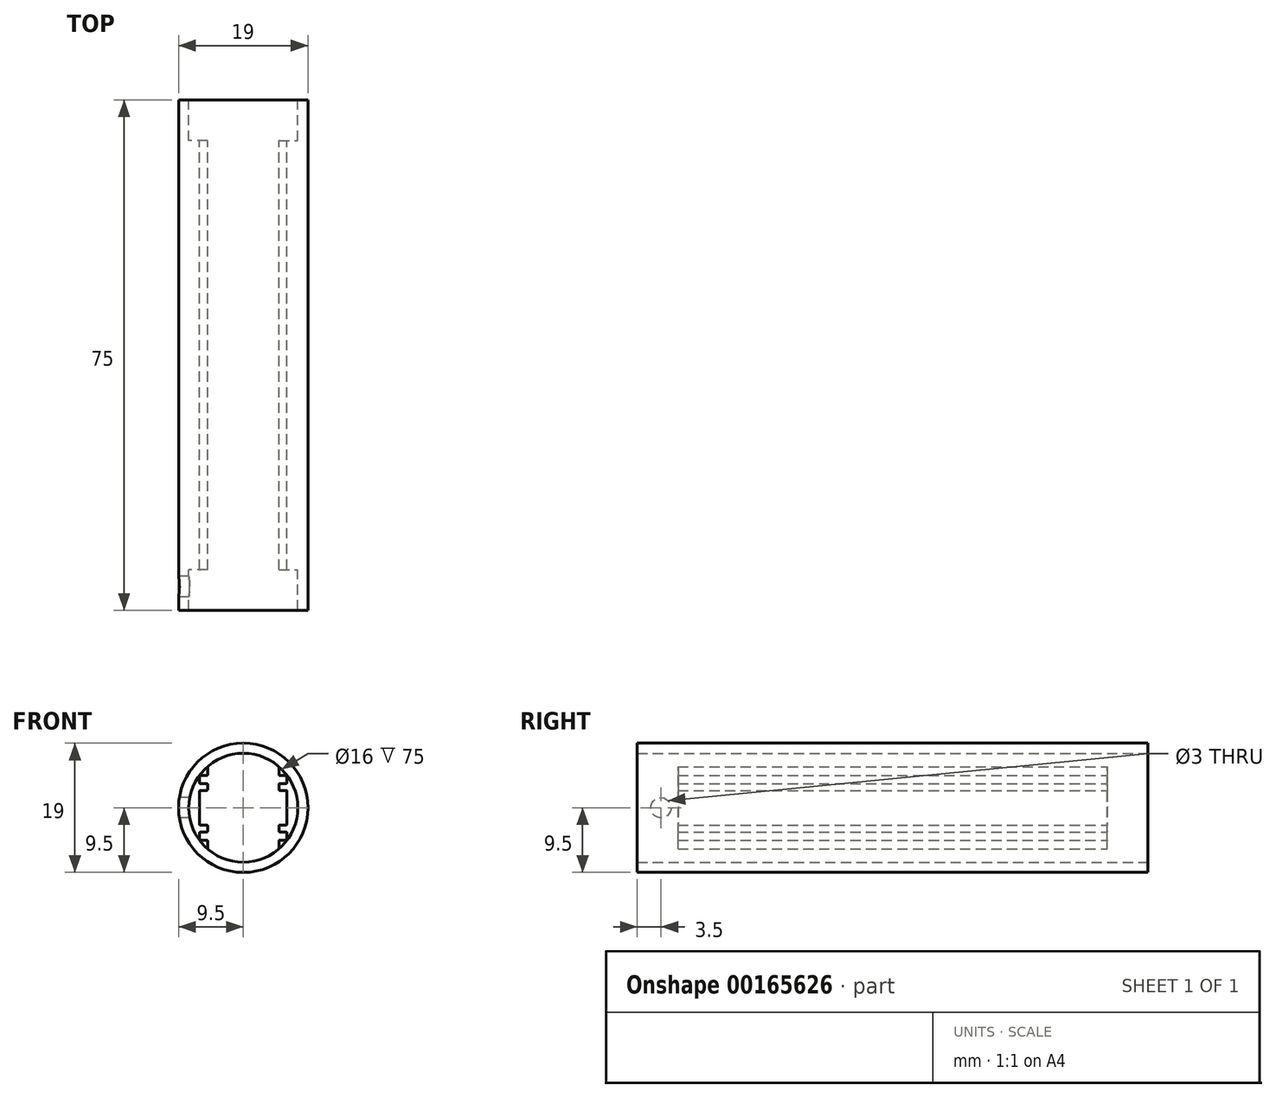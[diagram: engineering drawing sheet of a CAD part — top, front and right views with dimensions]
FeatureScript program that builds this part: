
annotation { "Feature Type Name" : "Feature", "Feature Type Description" : "" }
export const myFeature = defineFeature(function(context is Context, id is Id, definition is map)
    precondition{}
    {
        {
            assignVariable(context, id + "F0", {"name" : "Main_Diam", "anyValue" : 19});
        }
        {
            assignVariable(context, id + "F1", {"name" : "Main_Length", "anyValue" : 75});
        }
        {
            assignVariable(context, id + "F2", {"name" : "Bore_Depth_F", "anyValue" : 6});
        }
        {
            assignVariable(context, id + "F3", {"name" : "Bore_Depth_R", "anyValue" : 6});
        }
        {
            var Q0;
            Q0=qCreatedBy(makeId("Front.planeOp"),FACE);
            var sketch = newSketch(context, id + "F4", { "sketchPlane" : qUnion([Q0])});
            skLineSegment(sketch, "E0", {"start": v(-5.25, -3.45) * mm, "end": v(-5.25, -2.65) * mm});
            skLineSegment(sketch, "E1", {"start": v(9.2, 1.38) * mm, "end": v(9.42, 1.2) * mm});
            skArc(sketch, "E2", {"start": v(-5.35, -2.55) * mm, "mid": v(-5.28, -2.58) * mm, "end": v(-5.25, -2.65) * mm});
            skArc(sketch, "E3", {"start": v(6.3, 4.75) * mm, "mid": v(6.37, 4.72) * mm, "end": v(6.4, 4.65) * mm});
            skArc(sketch, "E4", {"start": v(-5.25, -6.04) * mm, "mid": v(0, -8) * mm, "end": v(5.25, -6.04) * mm});
            skLineSegment(sketch, "E5", {"start": v(1.53, 9.17) * mm, "end": v(1.78, 9.33) * mm});
            skLineSegment(sketch, "E6", {"start": v(-7.18, -5.91) * mm, "end": v(-7.2, -6.2) * mm});
            skArc(sketch, "E7", {"start": v(-8.33, -4.58) * mm, "mid": v(-8.23, -4.75) * mm, "end": v(-8.13, -4.92) * mm});
            skLineSegment(sketch, "E8", {"start": v(5.13, 7.76) * mm, "end": v(5.42, 7.8) * mm});
            skLineSegment(sketch, "E9", {"start": v(6.4, -2.45) * mm, "end": v(6.4, 0) * mm});
            skLineSegment(sketch, "E10", {"start": v(-2.33, -9) * mm, "end": v(-2.17, -9.25) * mm});
            skArc(sketch, "E11", {"start": v(8.97, -3.13) * mm, "mid": v(9.04, -2.94) * mm, "end": v(9.1, -2.74) * mm});
            skArc(sketch, "E12", {"start": v(-4.05, -8.6) * mm, "mid": v(-3.86, -8.68) * mm, "end": v(-3.68, -8.76) * mm});
            skArc(sketch, "E13", {"start": v(4.05, 8.6) * mm, "mid": v(3.86, 8.68) * mm, "end": v(3.68, 8.76) * mm});
            skLineSegment(sketch, "E14", {"start": v(6.63, 6.52) * mm, "end": v(6.92, 6.5) * mm});
            skArc(sketch, "E15", {"start": v(-6.4, 3.65) * mm, "mid": v(-6.37, 3.58) * mm, "end": v(-6.3, 3.55) * mm});
            skArc(sketch, "E16", {"start": v(5.74, 7.57) * mm, "mid": v(5.58, 7.69) * mm, "end": v(5.42, 7.8) * mm});
            skLineSegment(sketch, "E17", {"start": v(-9.2, 1.38) * mm, "end": v(-9.42, 1.2) * mm});
            skArc(sketch, "E18", {"start": v(1.78, -9.33) * mm, "mid": v(1.98, -9.3) * mm, "end": v(2.17, -9.25) * mm});
            skLineSegment(sketch, "E19", {"start": v(-5.8, 7.28) * mm, "end": v(-5.74, 7.57) * mm});
            skArc(sketch, "E20", {"start": v(-2.17, -9.25) * mm, "mid": v(-1.98, -9.3) * mm, "end": v(-1.78, -9.33) * mm});
            skLineSegment(sketch, "E21", {"start": v(7.84, 5) * mm, "end": v(8.13, 4.92) * mm});
            skLineSegment(sketch, "E22", {"start": v(2.33, 9) * mm, "end": v(2.17, 9.25) * mm});
            skArc(sketch, "E23", {"start": v(5.25, -3.45) * mm, "mid": v(5.28, -3.52) * mm, "end": v(5.35, -3.55) * mm});
            skLineSegment(sketch, "E24", {"start": v(5.8, -7.28) * mm, "end": v(5.74, -7.57) * mm});
            skArc(sketch, "E25", {"start": v(5.35, 2.55) * mm, "mid": v(5.28, 2.58) * mm, "end": v(5.25, 2.65) * mm});
            skArc(sketch, "E26", {"start": v(4.15, -8.32) * mm, "mid": v(4.65, -8.05) * mm, "end": v(5.13, -7.76) * mm});
            skArc(sketch, "E27", {"start": v(-5.35, 4.75) * mm, "mid": v(-5.28, 4.78) * mm, "end": v(-5.25, 4.85) * mm});
            skArc(sketch, "E28", {"start": v(-8.13, 4.92) * mm, "mid": v(-8.23, 4.75) * mm, "end": v(-8.33, 4.58) * mm});
            skLineSegment(sketch, "E29", {"start": v(7.84, -5) * mm, "end": v(8.13, -4.92) * mm});
            skArc(sketch, "E30", {"start": v(8.33, 4.58) * mm, "mid": v(8.23, 4.75) * mm, "end": v(8.13, 4.92) * mm});
            skLineSegment(sketch, "E31", {"start": v(-6.3, 3.55) * mm, "end": v(-5.35, 3.55) * mm});
            skLineSegment(sketch, "E32", {"start": v(-5.25, 3.45) * mm, "end": v(-5.25, 2.65) * mm});
            skArc(sketch, "E33", {"start": v(9.1, 2.74) * mm, "mid": v(9.04, 2.94) * mm, "end": v(8.97, 3.13) * mm});
            skLineSegment(sketch, "E34", {"start": v(6.3, 3.55) * mm, "end": v(5.35, 3.55) * mm});
            skLineSegment(sketch, "E35", {"start": v(4.15, -8.32) * mm, "end": v(4.05, -8.6) * mm});
            skLineSegment(sketch, "E36", {"start": v(5.25, 6.04) * mm, "end": v(5.25, 4.85) * mm});
            skArc(sketch, "E37", {"start": v(8.71, 3.26) * mm, "mid": v(8.5, 3.78) * mm, "end": v(8.25, 4.3) * mm});
            skArc(sketch, "E38", {"start": v(0.4, -9.3) * mm, "mid": v(0.97, -9.25) * mm, "end": v(1.53, -9.17) * mm});
            skArc(sketch, "E39", {"start": v(9.47, 0.8) * mm, "mid": v(9.45, 1) * mm, "end": v(9.42, 1.2) * mm});
            skArc(sketch, "E40", {"start": v(-4.15, 8.32) * mm, "mid": v(-4.65, 8.05) * mm, "end": v(-5.13, 7.76) * mm});
            skLineSegment(sketch, "E41", {"start": v(-0.4, 9.3) * mm, "end": v(-0.2, 9.5) * mm});
            skLineSegment(sketch, "E42", {"start": v(8.25, 4.3) * mm, "end": v(8.33, 4.58) * mm});
            skLineSegment(sketch, "E43", {"start": v(2.33, -9) * mm, "end": v(2.17, -9.25) * mm});
            skArc(sketch, "E44", {"start": v(-0.4, 9.3) * mm, "mid": v(-0.97, 9.25) * mm, "end": v(-1.53, 9.17) * mm});
            skLineSegment(sketch, "E45", {"start": v(-5.13, 7.76) * mm, "end": v(-5.42, 7.8) * mm});
            skLineSegment(sketch, "E46", {"start": v(-2.33, 9) * mm, "end": v(-2.17, 9.25) * mm});
            skLineSegment(sketch, "E47", {"start": v(6.63, -6.52) * mm, "end": v(6.92, -6.5) * mm});
            skArc(sketch, "E48", {"start": v(9.42, -1.2) * mm, "mid": v(9.45, -1) * mm, "end": v(9.47, -0.8) * mm});
            skArc(sketch, "E49", {"start": v(-3.68, 8.76) * mm, "mid": v(-3.86, 8.68) * mm, "end": v(-4.05, 8.6) * mm});
            skArc(sketch, "E50", {"start": v(9.2, 1.38) * mm, "mid": v(9.1, 1.93) * mm, "end": v(8.96, 2.48) * mm});
            skArc(sketch, "E51", {"start": v(5.35, 4.75) * mm, "mid": v(5.28, 4.78) * mm, "end": v(5.25, 4.85) * mm});
            skLineSegment(sketch, "E52", {"start": v(5.25, 3.45) * mm, "end": v(5.25, 2.65) * mm});
            skArc(sketch, "E53", {"start": v(-0.2, -9.5) * mm, "mid": v(0, -9.5) * mm, "end": v(0.2, -9.5) * mm});
            skArc(sketch, "E54", {"start": v(7.2, 6.2) * mm, "mid": v(7.06, 6.36) * mm, "end": v(6.92, 6.5) * mm});
            skLineSegment(sketch, "E55", {"start": v(3.4, 8.65) * mm, "end": v(3.68, 8.76) * mm});
            skArc(sketch, "E56", {"start": v(6.4, 3.65) * mm, "mid": v(6.37, 3.58) * mm, "end": v(6.3, 3.55) * mm});
            skLineSegment(sketch, "E57", {"start": v(-6.4, -2.45) * mm, "end": v(-6.4, 0) * mm});
            skArc(sketch, "E58", {"start": v(-2.33, 9) * mm, "mid": v(-2.87, 8.84) * mm, "end": v(-3.4, 8.65) * mm});
            skLineSegment(sketch, "E59", {"start": v(-1.53, 9.17) * mm, "end": v(-1.78, 9.33) * mm});
            skLineSegment(sketch, "E60", {"start": v(0.4, -9.3) * mm, "end": v(0.2, -9.5) * mm});
            skArc(sketch, "E61", {"start": v(-6.92, 6.5) * mm, "mid": v(-7.06, 6.36) * mm, "end": v(-7.2, 6.2) * mm});
            skArc(sketch, "E62", {"start": v(-8.25, 4.3) * mm, "mid": v(-8.5, 3.78) * mm, "end": v(-8.71, 3.26) * mm});
            skArc(sketch, "E63", {"start": v(6.3, -4.75) * mm, "mid": v(6.37, -4.72) * mm, "end": v(6.4, -4.65) * mm});
            skLineSegment(sketch, "E64", {"start": v(-6.4, 4.65) * mm, "end": v(-6.4, 3.65) * mm});
            skLineSegment(sketch, "E65", {"start": v(-6.4, 2.45) * mm, "end": v(-6.4, 0) * mm});
            skArc(sketch, "E66", {"start": v(8.25, -4.3) * mm, "mid": v(8.5, -3.78) * mm, "end": v(8.71, -3.26) * mm});
            skArc(sketch, "E67", {"start": v(-6.3, 2.55) * mm, "mid": v(-6.37, 2.52) * mm, "end": v(-6.4, 2.45) * mm});
            skLineSegment(sketch, "E68", {"start": v(-5.25, 6.04) * mm, "end": v(-5.25, 4.85) * mm});
            skLineSegment(sketch, "E69", {"start": v(-5.35, 4.75) * mm, "end": v(-6.3, 4.75) * mm});
            skLineSegment(sketch, "E70", {"start": v(-5.35, 2.55) * mm, "end": v(-6.3, 2.55) * mm});
            skArc(sketch, "E71", {"start": v(-5.25, 3.45) * mm, "mid": v(-5.28, 3.52) * mm, "end": v(-5.35, 3.55) * mm});
            skArc(sketch, "E72", {"start": v(-5.35, 2.55) * mm, "mid": v(-5.28, 2.58) * mm, "end": v(-5.25, 2.65) * mm});
            skArc(sketch, "E73", {"start": v(-6.3, 4.75) * mm, "mid": v(-6.37, 4.72) * mm, "end": v(-6.4, 4.65) * mm});
            skArc(sketch, "E74", {"start": v(6.3, 2.55) * mm, "mid": v(6.37, 2.52) * mm, "end": v(6.4, 2.45) * mm});
            skLineSegment(sketch, "E75", {"start": v(5.35, 2.55) * mm, "end": v(6.3, 2.55) * mm});
            skArc(sketch, "E76", {"start": v(5.25, 3.45) * mm, "mid": v(5.28, 3.52) * mm, "end": v(5.35, 3.55) * mm});
            skArc(sketch, "E77", {"start": v(0.2, 9.5) * mm, "mid": v(0, 9.5) * mm, "end": v(-0.2, 9.5) * mm});
            skLineSegment(sketch, "E78", {"start": v(5.35, 4.75) * mm, "end": v(6.3, 4.75) * mm});
            skLineSegment(sketch, "E79", {"start": v(6.4, 2.45) * mm, "end": v(6.4, 0) * mm});
            skLineSegment(sketch, "E80", {"start": v(6.4, 4.65) * mm, "end": v(6.4, 3.65) * mm});
            skArc(sketch, "E81", {"start": v(-5.35, -4.75) * mm, "mid": v(-5.28, -4.78) * mm, "end": v(-5.25, -4.85) * mm});
            skLineSegment(sketch, "E82", {"start": v(-6.3, -3.55) * mm, "end": v(-5.35, -3.55) * mm});
            skLineSegment(sketch, "E83", {"start": v(-5.35, -2.55) * mm, "end": v(-6.3, -2.55) * mm});
            skArc(sketch, "E84", {"start": v(-5.25, -3.45) * mm, "mid": v(-5.28, -3.52) * mm, "end": v(-5.35, -3.55) * mm});
            skArc(sketch, "E85", {"start": v(-6.3, -2.55) * mm, "mid": v(-6.37, -2.52) * mm, "end": v(-6.4, -2.45) * mm});
            skArc(sketch, "E86", {"start": v(-6.4, -3.65) * mm, "mid": v(-6.37, -3.58) * mm, "end": v(-6.3, -3.55) * mm});
            skArc(sketch, "E87", {"start": v(-6.3, -4.75) * mm, "mid": v(-6.37, -4.72) * mm, "end": v(-6.4, -4.65) * mm});
            skArc(sketch, "E88", {"start": v(5.35, -2.55) * mm, "mid": v(5.28, -2.58) * mm, "end": v(5.25, -2.65) * mm});
            skLineSegment(sketch, "E89", {"start": v(-3.4, 8.65) * mm, "end": v(-3.68, 8.76) * mm});
            skArc(sketch, "E90", {"start": v(6.3, -2.55) * mm, "mid": v(6.37, -2.52) * mm, "end": v(6.4, -2.45) * mm});
            skLineSegment(sketch, "E91", {"start": v(5.35, -2.55) * mm, "end": v(6.3, -2.55) * mm});
            skArc(sketch, "E92", {"start": v(6.4, -3.65) * mm, "mid": v(6.37, -3.58) * mm, "end": v(6.3, -3.55) * mm});
            skLineSegment(sketch, "E93", {"start": v(6.3, -3.55) * mm, "end": v(5.35, -3.55) * mm});
            skArc(sketch, "E94", {"start": v(5.35, -4.75) * mm, "mid": v(5.28, -4.78) * mm, "end": v(5.25, -4.85) * mm});
            skLineSegment(sketch, "E95", {"start": v(-5.25, -6.04) * mm, "end": v(-5.25, -4.85) * mm});
            skLineSegment(sketch, "E96", {"start": v(5.25, -3.45) * mm, "end": v(5.25, -2.65) * mm});
            skLineSegment(sketch, "E97", {"start": v(6.4, -4.65) * mm, "end": v(6.4, -3.65) * mm});
            skLineSegment(sketch, "E98", {"start": v(-5.35, -4.75) * mm, "end": v(-6.3, -4.75) * mm});
            skArc(sketch, "E99", {"start": v(-8.97, 3.13) * mm, "mid": v(-9.04, 2.94) * mm, "end": v(-9.1, 2.74) * mm});
            skLineSegment(sketch, "E100", {"start": v(-6.4, -4.65) * mm, "end": v(-6.4, -3.65) * mm});
            skLineSegment(sketch, "E101", {"start": v(5.35, -4.75) * mm, "end": v(6.3, -4.75) * mm});
            skLineSegment(sketch, "E102", {"start": v(-7.84, 5) * mm, "end": v(-8.13, 4.92) * mm});
            skLineSegment(sketch, "E103", {"start": v(5.25, -6.04) * mm, "end": v(5.25, -4.85) * mm});
            skArc(sketch, "E104", {"start": v(5.25, 6.04) * mm, "mid": v(0, 8) * mm, "end": v(-5.25, 6.04) * mm});
            skLineSegment(sketch, "E105", {"start": v(-0.4, -9.3) * mm, "end": v(-0.2, -9.5) * mm});
            skArc(sketch, "E106", {"start": v(2.33, -9) * mm, "mid": v(2.87, -8.84) * mm, "end": v(3.4, -8.65) * mm});
            skLineSegment(sketch, "E107", {"start": v(1.53, -9.17) * mm, "end": v(1.78, -9.33) * mm});
            skArc(sketch, "E108", {"start": v(3.68, -8.76) * mm, "mid": v(3.86, -8.68) * mm, "end": v(4.05, -8.6) * mm});
            skArc(sketch, "E109", {"start": v(-9.1, -2.74) * mm, "mid": v(-9.04, -2.94) * mm, "end": v(-8.97, -3.13) * mm});
            skLineSegment(sketch, "E110", {"start": v(3.4, -8.65) * mm, "end": v(3.68, -8.76) * mm});
            skArc(sketch, "E111", {"start": v(5.8, -7.28) * mm, "mid": v(6.22, -6.91) * mm, "end": v(6.63, -6.52) * mm});
            skArc(sketch, "E112", {"start": v(5.42, -7.8) * mm, "mid": v(5.58, -7.69) * mm, "end": v(5.74, -7.57) * mm});
            skLineSegment(sketch, "E113", {"start": v(5.13, -7.76) * mm, "end": v(5.42, -7.8) * mm});
            skLineSegment(sketch, "E114", {"start": v(-5.13, -7.76) * mm, "end": v(-5.42, -7.8) * mm});
            skLineSegment(sketch, "E115", {"start": v(7.18, -5.91) * mm, "end": v(7.2, -6.2) * mm});
            skLineSegment(sketch, "E116", {"start": v(-6.63, -6.52) * mm, "end": v(-6.92, -6.5) * mm});
            skArc(sketch, "E117", {"start": v(8.13, -4.92) * mm, "mid": v(8.23, -4.75) * mm, "end": v(8.33, -4.58) * mm});
            skArc(sketch, "E118", {"start": v(6.92, -6.5) * mm, "mid": v(7.06, -6.36) * mm, "end": v(7.2, -6.2) * mm});
            skArc(sketch, "E119", {"start": v(-5.74, -7.57) * mm, "mid": v(-5.58, -7.69) * mm, "end": v(-5.42, -7.8) * mm});
            skArc(sketch, "E120", {"start": v(8.96, -2.48) * mm, "mid": v(9.1, -1.93) * mm, "end": v(9.2, -1.38) * mm});
            skLineSegment(sketch, "E121", {"start": v(8.96, -2.48) * mm, "end": v(9.1, -2.74) * mm});
            skLineSegment(sketch, "E122", {"start": v(8.71, -3.26) * mm, "end": v(8.97, -3.13) * mm});
            skArc(sketch, "E123", {"start": v(9.28, -0.57) * mm, "mid": v(9.3, 0) * mm, "end": v(9.28, 0.57) * mm});
            skLineSegment(sketch, "E124", {"start": v(9.28, -0.57) * mm, "end": v(9.47, -0.8) * mm});
            skLineSegment(sketch, "E125", {"start": v(-1.53, -9.17) * mm, "end": v(-1.78, -9.33) * mm});
            skLineSegment(sketch, "E126", {"start": v(9.2, -1.38) * mm, "end": v(9.42, -1.2) * mm});
            skLineSegment(sketch, "E127", {"start": v(8.71, 3.26) * mm, "end": v(8.97, 3.13) * mm});
            skLineSegment(sketch, "E128", {"start": v(8.96, 2.48) * mm, "end": v(9.1, 2.74) * mm});
            skArc(sketch, "E129", {"start": v(7.84, 5) * mm, "mid": v(7.52, 5.47) * mm, "end": v(7.18, 5.91) * mm});
            skArc(sketch, "E130", {"start": v(6.63, 6.52) * mm, "mid": v(6.22, 6.91) * mm, "end": v(5.8, 7.28) * mm});
            skLineSegment(sketch, "E131", {"start": v(7.18, 5.91) * mm, "end": v(7.2, 6.2) * mm});
            skArc(sketch, "E132", {"start": v(5.13, 7.76) * mm, "mid": v(4.65, 8.05) * mm, "end": v(4.15, 8.32) * mm});
            skLineSegment(sketch, "E133", {"start": v(5.8, 7.28) * mm, "end": v(5.74, 7.57) * mm});
            skArc(sketch, "E134", {"start": v(3.4, 8.65) * mm, "mid": v(2.87, 8.84) * mm, "end": v(2.33, 9) * mm});
            skLineSegment(sketch, "E135", {"start": v(4.15, 8.32) * mm, "end": v(4.05, 8.6) * mm});
            skArc(sketch, "E136", {"start": v(1.53, 9.17) * mm, "mid": v(0.97, 9.25) * mm, "end": v(0.4, 9.3) * mm});
            skArc(sketch, "E137", {"start": v(2.17, 9.25) * mm, "mid": v(1.98, 9.3) * mm, "end": v(1.78, 9.33) * mm});
            skLineSegment(sketch, "E138", {"start": v(0.4, 9.3) * mm, "end": v(0.2, 9.5) * mm});
            skArc(sketch, "E139", {"start": v(-1.78, 9.33) * mm, "mid": v(-1.98, 9.3) * mm, "end": v(-2.17, 9.25) * mm});
            skLineSegment(sketch, "E140", {"start": v(-4.15, 8.32) * mm, "end": v(-4.05, 8.6) * mm});
            skArc(sketch, "E141", {"start": v(-5.8, 7.28) * mm, "mid": v(-6.22, 6.91) * mm, "end": v(-6.63, 6.52) * mm});
            skArc(sketch, "E142", {"start": v(-5.42, 7.8) * mm, "mid": v(-5.58, 7.69) * mm, "end": v(-5.74, 7.57) * mm});
            skLineSegment(sketch, "E143", {"start": v(-9.2, -1.38) * mm, "end": v(-9.42, -1.2) * mm});
            skLineSegment(sketch, "E144", {"start": v(-7.18, 5.91) * mm, "end": v(-7.2, 6.2) * mm});
            skLineSegment(sketch, "E145", {"start": v(-6.63, 6.52) * mm, "end": v(-6.92, 6.5) * mm});
            skArc(sketch, "E146", {"start": v(-8.96, 2.48) * mm, "mid": v(-9.1, 1.93) * mm, "end": v(-9.2, 1.38) * mm});
            skLineSegment(sketch, "E147", {"start": v(-8.96, 2.48) * mm, "end": v(-9.1, 2.74) * mm});
            skLineSegment(sketch, "E148", {"start": v(-8.71, 3.26) * mm, "end": v(-8.97, 3.13) * mm});
            skArc(sketch, "E149", {"start": v(-9.28, 0.57) * mm, "mid": v(-9.3, 0) * mm, "end": v(-9.28, -0.57) * mm});
            skArc(sketch, "E150", {"start": v(-9.42, 1.2) * mm, "mid": v(-9.45, 1) * mm, "end": v(-9.47, 0.8) * mm});
            skLineSegment(sketch, "E151", {"start": v(-9.28, 0.57) * mm, "end": v(-9.47, 0.8) * mm});
            skLineSegment(sketch, "E152", {"start": v(8.25, -4.3) * mm, "end": v(8.33, -4.58) * mm});
            skArc(sketch, "E153", {"start": v(-9.2, -1.38) * mm, "mid": v(-9.1, -1.93) * mm, "end": v(-8.96, -2.48) * mm});
            skArc(sketch, "E154", {"start": v(-9.47, -0.8) * mm, "mid": v(-9.45, -1) * mm, "end": v(-9.42, -1.2) * mm});
            skLineSegment(sketch, "E155", {"start": v(-9.28, -0.57) * mm, "end": v(-9.47, -0.8) * mm});
            skArc(sketch, "E156", {"start": v(-8.71, -3.26) * mm, "mid": v(-8.5, -3.78) * mm, "end": v(-8.25, -4.3) * mm});
            skLineSegment(sketch, "E157", {"start": v(-8.71, -3.26) * mm, "end": v(-8.97, -3.13) * mm});
            skLineSegment(sketch, "E158", {"start": v(-8.96, -2.48) * mm, "end": v(-9.1, -2.74) * mm});
            skArc(sketch, "E159", {"start": v(-7.84, -5) * mm, "mid": v(-7.52, -5.47) * mm, "end": v(-7.18, -5.91) * mm});
            skLineSegment(sketch, "E160", {"start": v(-7.84, -5) * mm, "end": v(-8.13, -4.92) * mm});
            skLineSegment(sketch, "E161", {"start": v(-8.25, -4.3) * mm, "end": v(-8.33, -4.58) * mm});
            skArc(sketch, "E162", {"start": v(-6.63, -6.52) * mm, "mid": v(-6.22, -6.91) * mm, "end": v(-5.8, -7.28) * mm});
            skLineSegment(sketch, "E163", {"start": v(9.28, 0.57) * mm, "end": v(9.47, 0.8) * mm});
            skArc(sketch, "E164", {"start": v(-7.2, -6.2) * mm, "mid": v(-7.06, -6.36) * mm, "end": v(-6.92, -6.5) * mm});
            skArc(sketch, "E165", {"start": v(7.18, -5.91) * mm, "mid": v(7.52, -5.47) * mm, "end": v(7.84, -5) * mm});
            skLineSegment(sketch, "E166", {"start": v(-5.8, -7.28) * mm, "end": v(-5.74, -7.57) * mm});
            skArc(sketch, "E167", {"start": v(-3.4, -8.65) * mm, "mid": v(-2.87, -8.84) * mm, "end": v(-2.33, -9) * mm});
            skLineSegment(sketch, "E168", {"start": v(-3.4, -8.65) * mm, "end": v(-3.68, -8.76) * mm});
            skLineSegment(sketch, "E169", {"start": v(-4.15, -8.32) * mm, "end": v(-4.05, -8.6) * mm});
            skArc(sketch, "E170", {"start": v(-1.53, -9.17) * mm, "mid": v(-0.97, -9.25) * mm, "end": v(-0.4, -9.3) * mm});
            skArc(sketch, "E171", {"start": v(-7.18, 5.91) * mm, "mid": v(-7.52, 5.47) * mm, "end": v(-7.84, 5) * mm});
            skLineSegment(sketch, "E172", {"start": v(-8.25, 4.3) * mm, "end": v(-8.33, 4.58) * mm});
            skArc(sketch, "E173", {"start": v(-5.13, -7.76) * mm, "mid": v(-4.65, -8.05) * mm, "end": v(-4.15, -8.32) * mm});
            skSolve(sketch);
        }
        {
            var Q0;
            Q0=makeQuery(id+"F4.imprint","IMPRINT",FACE,{"disambiguationData":[TD([[makeQuery(id+"F4.imprint","IMPRINT",EDGE,{"derivedFrom":sQuery(id+"F4.wireOp",EDGE,"E0")}),1.0]])]});
            extrude(context, id + "F5", {"entities" : qUnion([Q0]), "depth" : (getVariable(context, 'Main_Length') - getVariable(context, 'Bore_Depth_F') - getVariable(context, 'Bore_Depth_R')) * mm});
        }
        {
            var Q0;
            Q0=makeQuery(id+"F5.opExtrude","CAP_FACE",FACE,{"disambiguationData":[OSD([sQuery(id+"F4.wireOp",EDGE,"E0"),sQuery(id+"F4.wireOp",EDGE,"E1"),sQuery(id+"F4.wireOp",EDGE,"E2"),sQuery(id+"F4.wireOp",EDGE,"E3"),sQuery(id+"F4.wireOp",EDGE,"E4"),sQuery(id+"F4.wireOp",EDGE,"E5"),sQuery(id+"F4.wireOp",EDGE,"E6"),sQuery(id+"F4.wireOp",EDGE,"E7"),sQuery(id+"F4.wireOp",EDGE,"E8"),sQuery(id+"F4.wireOp",EDGE,"E9"),sQuery(id+"F4.wireOp",EDGE,"E10"),sQuery(id+"F4.wireOp",EDGE,"E11"),sQuery(id+"F4.wireOp",EDGE,"E12"),sQuery(id+"F4.wireOp",EDGE,"E13"),sQuery(id+"F4.wireOp",EDGE,"E14"),sQuery(id+"F4.wireOp",EDGE,"E15"),sQuery(id+"F4.wireOp",EDGE,"E16"),sQuery(id+"F4.wireOp",EDGE,"E17"),sQuery(id+"F4.wireOp",EDGE,"E18"),sQuery(id+"F4.wireOp",EDGE,"E19"),sQuery(id+"F4.wireOp",EDGE,"E20"),sQuery(id+"F4.wireOp",EDGE,"E21"),sQuery(id+"F4.wireOp",EDGE,"E22"),sQuery(id+"F4.wireOp",EDGE,"E23"),sQuery(id+"F4.wireOp",EDGE,"E24"),sQuery(id+"F4.wireOp",EDGE,"E25"),sQuery(id+"F4.wireOp",EDGE,"E26"),sQuery(id+"F4.wireOp",EDGE,"E27"),sQuery(id+"F4.wireOp",EDGE,"E28"),sQuery(id+"F4.wireOp",EDGE,"E29"),sQuery(id+"F4.wireOp",EDGE,"E30"),sQuery(id+"F4.wireOp",EDGE,"E31"),sQuery(id+"F4.wireOp",EDGE,"E32"),sQuery(id+"F4.wireOp",EDGE,"E33"),sQuery(id+"F4.wireOp",EDGE,"E34"),sQuery(id+"F4.wireOp",EDGE,"E35"),sQuery(id+"F4.wireOp",EDGE,"E36"),sQuery(id+"F4.wireOp",EDGE,"E37"),sQuery(id+"F4.wireOp",EDGE,"E38"),sQuery(id+"F4.wireOp",EDGE,"E39"),sQuery(id+"F4.wireOp",EDGE,"E40"),sQuery(id+"F4.wireOp",EDGE,"E41"),sQuery(id+"F4.wireOp",EDGE,"E42"),sQuery(id+"F4.wireOp",EDGE,"E43"),sQuery(id+"F4.wireOp",EDGE,"E44"),sQuery(id+"F4.wireOp",EDGE,"E45"),sQuery(id+"F4.wireOp",EDGE,"E46"),sQuery(id+"F4.wireOp",EDGE,"E47"),sQuery(id+"F4.wireOp",EDGE,"E48"),sQuery(id+"F4.wireOp",EDGE,"E49"),sQuery(id+"F4.wireOp",EDGE,"E50"),sQuery(id+"F4.wireOp",EDGE,"E51"),sQuery(id+"F4.wireOp",EDGE,"E52"),sQuery(id+"F4.wireOp",EDGE,"E53"),sQuery(id+"F4.wireOp",EDGE,"E54"),sQuery(id+"F4.wireOp",EDGE,"E55"),sQuery(id+"F4.wireOp",EDGE,"E56"),sQuery(id+"F4.wireOp",EDGE,"E57"),sQuery(id+"F4.wireOp",EDGE,"E58"),sQuery(id+"F4.wireOp",EDGE,"E59"),sQuery(id+"F4.wireOp",EDGE,"E60"),sQuery(id+"F4.wireOp",EDGE,"E61"),sQuery(id+"F4.wireOp",EDGE,"E62"),sQuery(id+"F4.wireOp",EDGE,"E63"),sQuery(id+"F4.wireOp",EDGE,"E64"),sQuery(id+"F4.wireOp",EDGE,"E65"),sQuery(id+"F4.wireOp",EDGE,"E66"),sQuery(id+"F4.wireOp",EDGE,"E67"),sQuery(id+"F4.wireOp",EDGE,"E68"),sQuery(id+"F4.wireOp",EDGE,"E69"),sQuery(id+"F4.wireOp",EDGE,"E70"),sQuery(id+"F4.wireOp",EDGE,"E71"),sQuery(id+"F4.wireOp",EDGE,"E72"),sQuery(id+"F4.wireOp",EDGE,"E73"),sQuery(id+"F4.wireOp",EDGE,"E74"),sQuery(id+"F4.wireOp",EDGE,"E75"),sQuery(id+"F4.wireOp",EDGE,"E76"),sQuery(id+"F4.wireOp",EDGE,"E77"),sQuery(id+"F4.wireOp",EDGE,"E78"),sQuery(id+"F4.wireOp",EDGE,"E79"),sQuery(id+"F4.wireOp",EDGE,"E80"),sQuery(id+"F4.wireOp",EDGE,"E81"),sQuery(id+"F4.wireOp",EDGE,"E82"),sQuery(id+"F4.wireOp",EDGE,"E83"),sQuery(id+"F4.wireOp",EDGE,"E84"),sQuery(id+"F4.wireOp",EDGE,"E85"),sQuery(id+"F4.wireOp",EDGE,"E86"),sQuery(id+"F4.wireOp",EDGE,"E87"),sQuery(id+"F4.wireOp",EDGE,"E88"),sQuery(id+"F4.wireOp",EDGE,"E89"),sQuery(id+"F4.wireOp",EDGE,"E90"),sQuery(id+"F4.wireOp",EDGE,"E91"),sQuery(id+"F4.wireOp",EDGE,"E92"),sQuery(id+"F4.wireOp",EDGE,"E93"),sQuery(id+"F4.wireOp",EDGE,"E94"),sQuery(id+"F4.wireOp",EDGE,"E95"),sQuery(id+"F4.wireOp",EDGE,"E96"),sQuery(id+"F4.wireOp",EDGE,"E97"),sQuery(id+"F4.wireOp",EDGE,"E98"),sQuery(id+"F4.wireOp",EDGE,"E99"),sQuery(id+"F4.wireOp",EDGE,"E100"),sQuery(id+"F4.wireOp",EDGE,"E101"),sQuery(id+"F4.wireOp",EDGE,"E102"),sQuery(id+"F4.wireOp",EDGE,"E103"),sQuery(id+"F4.wireOp",EDGE,"E104"),sQuery(id+"F4.wireOp",EDGE,"E105"),sQuery(id+"F4.wireOp",EDGE,"E106"),sQuery(id+"F4.wireOp",EDGE,"E107"),sQuery(id+"F4.wireOp",EDGE,"E108"),sQuery(id+"F4.wireOp",EDGE,"E109"),sQuery(id+"F4.wireOp",EDGE,"E110"),sQuery(id+"F4.wireOp",EDGE,"E111"),sQuery(id+"F4.wireOp",EDGE,"E112"),sQuery(id+"F4.wireOp",EDGE,"E113"),sQuery(id+"F4.wireOp",EDGE,"E114"),sQuery(id+"F4.wireOp",EDGE,"E115"),sQuery(id+"F4.wireOp",EDGE,"E116"),sQuery(id+"F4.wireOp",EDGE,"E117"),sQuery(id+"F4.wireOp",EDGE,"E118"),sQuery(id+"F4.wireOp",EDGE,"E119"),sQuery(id+"F4.wireOp",EDGE,"E120"),sQuery(id+"F4.wireOp",EDGE,"E121"),sQuery(id+"F4.wireOp",EDGE,"E122"),sQuery(id+"F4.wireOp",EDGE,"E123"),sQuery(id+"F4.wireOp",EDGE,"E124"),sQuery(id+"F4.wireOp",EDGE,"E125"),sQuery(id+"F4.wireOp",EDGE,"E126"),sQuery(id+"F4.wireOp",EDGE,"E127"),sQuery(id+"F4.wireOp",EDGE,"E128"),sQuery(id+"F4.wireOp",EDGE,"E129"),sQuery(id+"F4.wireOp",EDGE,"E130"),sQuery(id+"F4.wireOp",EDGE,"E131"),sQuery(id+"F4.wireOp",EDGE,"E132"),sQuery(id+"F4.wireOp",EDGE,"E133"),sQuery(id+"F4.wireOp",EDGE,"E134"),sQuery(id+"F4.wireOp",EDGE,"E135"),sQuery(id+"F4.wireOp",EDGE,"E136"),sQuery(id+"F4.wireOp",EDGE,"E137"),sQuery(id+"F4.wireOp",EDGE,"E138"),sQuery(id+"F4.wireOp",EDGE,"E139"),sQuery(id+"F4.wireOp",EDGE,"E140"),sQuery(id+"F4.wireOp",EDGE,"E141"),sQuery(id+"F4.wireOp",EDGE,"E142"),sQuery(id+"F4.wireOp",EDGE,"E143"),sQuery(id+"F4.wireOp",EDGE,"E144"),sQuery(id+"F4.wireOp",EDGE,"E145"),sQuery(id+"F4.wireOp",EDGE,"E146"),sQuery(id+"F4.wireOp",EDGE,"E147"),sQuery(id+"F4.wireOp",EDGE,"E148"),sQuery(id+"F4.wireOp",EDGE,"E149"),sQuery(id+"F4.wireOp",EDGE,"E150"),sQuery(id+"F4.wireOp",EDGE,"E151"),sQuery(id+"F4.wireOp",EDGE,"E152"),sQuery(id+"F4.wireOp",EDGE,"E153"),sQuery(id+"F4.wireOp",EDGE,"E154"),sQuery(id+"F4.wireOp",EDGE,"E155"),sQuery(id+"F4.wireOp",EDGE,"E156"),sQuery(id+"F4.wireOp",EDGE,"E157"),sQuery(id+"F4.wireOp",EDGE,"E158"),sQuery(id+"F4.wireOp",EDGE,"E159"),sQuery(id+"F4.wireOp",EDGE,"E160"),sQuery(id+"F4.wireOp",EDGE,"E161"),sQuery(id+"F4.wireOp",EDGE,"E162"),sQuery(id+"F4.wireOp",EDGE,"E163"),sQuery(id+"F4.wireOp",EDGE,"E164"),sQuery(id+"F4.wireOp",EDGE,"E165"),sQuery(id+"F4.wireOp",EDGE,"E166"),sQuery(id+"F4.wireOp",EDGE,"E167"),sQuery(id+"F4.wireOp",EDGE,"E168"),sQuery(id+"F4.wireOp",EDGE,"E169"),sQuery(id+"F4.wireOp",EDGE,"E170"),sQuery(id+"F4.wireOp",EDGE,"E171"),sQuery(id+"F4.wireOp",EDGE,"E172"),sQuery(id+"F4.wireOp",EDGE,"E173")])],"isStart":false});
            var sketch = newSketch(context, id + "F6", { "sketchPlane" : qUnion([Q0])});
            skCircle(sketch, "E174", {"center": v(0, 0) * mm, "radius": 8 * mm});
            skLineSegment(sketch, "E175.0.0", {"start": v(9.42, 1.2) * mm, "end": v(9.2, 1.38) * mm});
            skArc(sketch, "E175.0.1", {"start": v(9.2, 1.38) * mm, "mid": v(9.1, 1.93) * mm, "end": v(8.96, 2.48) * mm});
            skLineSegment(sketch, "E175.0.2", {"start": v(8.96, 2.48) * mm, "end": v(9.1, 2.74) * mm});
            skArc(sketch, "E175.0.3", {"start": v(9.1, 2.74) * mm, "mid": v(9.04, 2.94) * mm, "end": v(8.97, 3.13) * mm});
            skLineSegment(sketch, "E175.0.4", {"start": v(8.97, 3.13) * mm, "end": v(8.71, 3.26) * mm});
            skArc(sketch, "E175.0.5", {"start": v(8.71, 3.26) * mm, "mid": v(8.5, 3.78) * mm, "end": v(8.25, 4.3) * mm});
            skLineSegment(sketch, "E175.0.6", {"start": v(8.25, 4.3) * mm, "end": v(8.33, 4.58) * mm});
            skArc(sketch, "E175.0.7", {"start": v(8.33, 4.58) * mm, "mid": v(8.23, 4.75) * mm, "end": v(8.13, 4.92) * mm});
            skLineSegment(sketch, "E175.0.8", {"start": v(8.13, 4.92) * mm, "end": v(7.84, 5) * mm});
            skArc(sketch, "E175.0.9", {"start": v(7.84, 5) * mm, "mid": v(7.52, 5.47) * mm, "end": v(7.18, 5.91) * mm});
            skLineSegment(sketch, "E175.0.10", {"start": v(7.18, 5.91) * mm, "end": v(7.2, 6.2) * mm});
            skArc(sketch, "E175.0.11", {"start": v(7.2, 6.2) * mm, "mid": v(7.06, 6.36) * mm, "end": v(6.92, 6.5) * mm});
            skLineSegment(sketch, "E175.0.12", {"start": v(6.92, 6.5) * mm, "end": v(6.63, 6.52) * mm});
            skArc(sketch, "E175.0.13", {"start": v(6.63, 6.52) * mm, "mid": v(6.22, 6.91) * mm, "end": v(5.8, 7.28) * mm});
            skLineSegment(sketch, "E175.0.14", {"start": v(5.8, 7.28) * mm, "end": v(5.74, 7.57) * mm});
            skArc(sketch, "E175.0.15", {"start": v(5.74, 7.57) * mm, "mid": v(5.58, 7.69) * mm, "end": v(5.42, 7.8) * mm});
            skLineSegment(sketch, "E175.0.16", {"start": v(5.42, 7.8) * mm, "end": v(5.13, 7.76) * mm});
            skArc(sketch, "E175.0.17", {"start": v(5.13, 7.76) * mm, "mid": v(4.65, 8.05) * mm, "end": v(4.15, 8.32) * mm});
            skLineSegment(sketch, "E175.0.18", {"start": v(4.15, 8.32) * mm, "end": v(4.05, 8.6) * mm});
            skArc(sketch, "E175.0.19", {"start": v(4.05, 8.6) * mm, "mid": v(3.86, 8.68) * mm, "end": v(3.68, 8.76) * mm});
            skLineSegment(sketch, "E175.0.20", {"start": v(3.68, 8.76) * mm, "end": v(3.4, 8.65) * mm});
            skArc(sketch, "E175.0.21", {"start": v(3.4, 8.65) * mm, "mid": v(2.87, 8.84) * mm, "end": v(2.33, 9) * mm});
            skLineSegment(sketch, "E175.0.22", {"start": v(2.33, 9) * mm, "end": v(2.17, 9.25) * mm});
            skArc(sketch, "E175.0.23", {"start": v(2.17, 9.25) * mm, "mid": v(1.98, 9.3) * mm, "end": v(1.78, 9.33) * mm});
            skLineSegment(sketch, "E175.0.24", {"start": v(1.78, 9.33) * mm, "end": v(1.53, 9.17) * mm});
            skArc(sketch, "E175.0.25", {"start": v(1.53, 9.17) * mm, "mid": v(0.97, 9.25) * mm, "end": v(0.4, 9.3) * mm});
            skLineSegment(sketch, "E175.0.26", {"start": v(0.4, 9.3) * mm, "end": v(0.2, 9.5) * mm});
            skArc(sketch, "E175.0.27", {"start": v(0.2, 9.5) * mm, "mid": v(0, 9.5) * mm, "end": v(-0.2, 9.5) * mm});
            skLineSegment(sketch, "E175.0.28", {"start": v(-0.2, 9.5) * mm, "end": v(-0.4, 9.3) * mm});
            skArc(sketch, "E175.0.29", {"start": v(-0.4, 9.3) * mm, "mid": v(-0.97, 9.25) * mm, "end": v(-1.53, 9.17) * mm});
            skLineSegment(sketch, "E175.0.30", {"start": v(-1.53, 9.17) * mm, "end": v(-1.78, 9.33) * mm});
            skArc(sketch, "E175.0.31", {"start": v(-1.78, 9.33) * mm, "mid": v(-1.98, 9.3) * mm, "end": v(-2.17, 9.25) * mm});
            skLineSegment(sketch, "E175.0.32", {"start": v(-2.17, 9.25) * mm, "end": v(-2.33, 9) * mm});
            skArc(sketch, "E175.0.33", {"start": v(-2.33, 9) * mm, "mid": v(-2.87, 8.84) * mm, "end": v(-3.4, 8.65) * mm});
            skLineSegment(sketch, "E175.0.34", {"start": v(-3.4, 8.65) * mm, "end": v(-3.68, 8.76) * mm});
            skArc(sketch, "E175.0.35", {"start": v(-3.68, 8.76) * mm, "mid": v(-3.86, 8.68) * mm, "end": v(-4.05, 8.6) * mm});
            skLineSegment(sketch, "E175.0.36", {"start": v(-4.05, 8.6) * mm, "end": v(-4.15, 8.32) * mm});
            skArc(sketch, "E175.0.37", {"start": v(-4.15, 8.32) * mm, "mid": v(-4.65, 8.05) * mm, "end": v(-5.13, 7.76) * mm});
            skLineSegment(sketch, "E175.0.38", {"start": v(-5.13, 7.76) * mm, "end": v(-5.42, 7.8) * mm});
            skArc(sketch, "E175.0.39", {"start": v(-5.42, 7.8) * mm, "mid": v(-5.58, 7.69) * mm, "end": v(-5.74, 7.57) * mm});
            skLineSegment(sketch, "E175.0.40", {"start": v(-5.74, 7.57) * mm, "end": v(-5.8, 7.28) * mm});
            skArc(sketch, "E175.0.41", {"start": v(-5.8, 7.28) * mm, "mid": v(-6.22, 6.91) * mm, "end": v(-6.63, 6.52) * mm});
            skLineSegment(sketch, "E175.0.42", {"start": v(-6.63, 6.52) * mm, "end": v(-6.92, 6.5) * mm});
            skArc(sketch, "E175.0.43", {"start": v(-6.92, 6.5) * mm, "mid": v(-7.06, 6.36) * mm, "end": v(-7.2, 6.2) * mm});
            skLineSegment(sketch, "E175.0.44", {"start": v(-7.2, 6.2) * mm, "end": v(-7.18, 5.91) * mm});
            skArc(sketch, "E175.0.45", {"start": v(-7.18, 5.91) * mm, "mid": v(-7.52, 5.47) * mm, "end": v(-7.84, 5) * mm});
            skLineSegment(sketch, "E175.0.46", {"start": v(-7.84, 5) * mm, "end": v(-8.13, 4.92) * mm});
            skArc(sketch, "E175.0.47", {"start": v(-8.13, 4.92) * mm, "mid": v(-8.23, 4.75) * mm, "end": v(-8.33, 4.58) * mm});
            skLineSegment(sketch, "E175.0.48", {"start": v(-8.33, 4.58) * mm, "end": v(-8.25, 4.3) * mm});
            skArc(sketch, "E175.0.49", {"start": v(-8.25, 4.3) * mm, "mid": v(-8.5, 3.78) * mm, "end": v(-8.71, 3.26) * mm});
            skLineSegment(sketch, "E175.0.50", {"start": v(-8.71, 3.26) * mm, "end": v(-8.97, 3.13) * mm});
            skArc(sketch, "E175.0.51", {"start": v(-8.97, 3.13) * mm, "mid": v(-9.04, 2.94) * mm, "end": v(-9.1, 2.74) * mm});
            skLineSegment(sketch, "E175.0.52", {"start": v(-9.1, 2.74) * mm, "end": v(-8.96, 2.48) * mm});
            skArc(sketch, "E175.0.53", {"start": v(-8.96, 2.48) * mm, "mid": v(-9.1, 1.93) * mm, "end": v(-9.2, 1.38) * mm});
            skLineSegment(sketch, "E175.0.54", {"start": v(-9.2, 1.38) * mm, "end": v(-9.42, 1.2) * mm});
            skArc(sketch, "E175.0.55", {"start": v(-9.42, 1.2) * mm, "mid": v(-9.45, 1) * mm, "end": v(-9.47, 0.8) * mm});
            skLineSegment(sketch, "E175.0.56", {"start": v(-9.47, 0.8) * mm, "end": v(-9.28, 0.57) * mm});
            skArc(sketch, "E175.0.57", {"start": v(-9.28, 0.57) * mm, "mid": v(-9.3, 0) * mm, "end": v(-9.28, -0.57) * mm});
            skLineSegment(sketch, "E175.0.58", {"start": v(-9.28, -0.57) * mm, "end": v(-9.47, -0.8) * mm});
            skArc(sketch, "E175.0.59", {"start": v(-9.47, -0.8) * mm, "mid": v(-9.45, -1) * mm, "end": v(-9.42, -1.2) * mm});
            skLineSegment(sketch, "E175.0.60", {"start": v(-9.42, -1.2) * mm, "end": v(-9.2, -1.38) * mm});
            skArc(sketch, "E175.0.61", {"start": v(-9.2, -1.38) * mm, "mid": v(-9.1, -1.93) * mm, "end": v(-8.96, -2.48) * mm});
            skLineSegment(sketch, "E175.0.62", {"start": v(-8.96, -2.48) * mm, "end": v(-9.1, -2.74) * mm});
            skArc(sketch, "E175.0.63", {"start": v(-9.1, -2.74) * mm, "mid": v(-9.04, -2.94) * mm, "end": v(-8.97, -3.13) * mm});
            skLineSegment(sketch, "E175.0.64", {"start": v(-8.97, -3.13) * mm, "end": v(-8.71, -3.26) * mm});
            skArc(sketch, "E175.0.65", {"start": v(-8.71, -3.26) * mm, "mid": v(-8.5, -3.78) * mm, "end": v(-8.25, -4.3) * mm});
            skLineSegment(sketch, "E175.0.66", {"start": v(-8.25, -4.3) * mm, "end": v(-8.33, -4.58) * mm});
            skArc(sketch, "E175.0.67", {"start": v(-8.33, -4.58) * mm, "mid": v(-8.23, -4.75) * mm, "end": v(-8.13, -4.92) * mm});
            skLineSegment(sketch, "E175.0.68", {"start": v(-8.13, -4.92) * mm, "end": v(-7.84, -5) * mm});
            skArc(sketch, "E175.0.69", {"start": v(-7.84, -5) * mm, "mid": v(-7.52, -5.47) * mm, "end": v(-7.18, -5.91) * mm});
            skLineSegment(sketch, "E175.0.70", {"start": v(-7.18, -5.91) * mm, "end": v(-7.2, -6.2) * mm});
            skArc(sketch, "E175.0.71", {"start": v(-7.2, -6.2) * mm, "mid": v(-7.06, -6.36) * mm, "end": v(-6.92, -6.5) * mm});
            skLineSegment(sketch, "E175.0.72", {"start": v(-6.92, -6.5) * mm, "end": v(-6.63, -6.52) * mm});
            skArc(sketch, "E175.0.73", {"start": v(-6.63, -6.52) * mm, "mid": v(-6.22, -6.91) * mm, "end": v(-5.8, -7.28) * mm});
            skLineSegment(sketch, "E175.0.74", {"start": v(-5.8, -7.28) * mm, "end": v(-5.74, -7.57) * mm});
            skArc(sketch, "E175.0.75", {"start": v(-5.74, -7.57) * mm, "mid": v(-5.58, -7.69) * mm, "end": v(-5.42, -7.8) * mm});
            skLineSegment(sketch, "E175.0.76", {"start": v(-5.42, -7.8) * mm, "end": v(-5.13, -7.76) * mm});
            skArc(sketch, "E175.0.77", {"start": v(-5.13, -7.76) * mm, "mid": v(-4.65, -8.05) * mm, "end": v(-4.15, -8.32) * mm});
            skLineSegment(sketch, "E175.0.78", {"start": v(-4.15, -8.32) * mm, "end": v(-4.05, -8.6) * mm});
            skArc(sketch, "E175.0.79", {"start": v(-4.05, -8.6) * mm, "mid": v(-3.86, -8.68) * mm, "end": v(-3.68, -8.76) * mm});
            skLineSegment(sketch, "E175.0.80", {"start": v(-3.68, -8.76) * mm, "end": v(-3.4, -8.65) * mm});
            skArc(sketch, "E175.0.81", {"start": v(-3.4, -8.65) * mm, "mid": v(-2.87, -8.84) * mm, "end": v(-2.33, -9) * mm});
            skLineSegment(sketch, "E175.0.82", {"start": v(-2.33, -9) * mm, "end": v(-2.17, -9.25) * mm});
            skArc(sketch, "E175.0.83", {"start": v(-2.17, -9.25) * mm, "mid": v(-1.98, -9.3) * mm, "end": v(-1.78, -9.33) * mm});
            skLineSegment(sketch, "E175.0.84", {"start": v(-1.78, -9.33) * mm, "end": v(-1.53, -9.17) * mm});
            skArc(sketch, "E175.0.85", {"start": v(-1.53, -9.17) * mm, "mid": v(-0.97, -9.25) * mm, "end": v(-0.4, -9.3) * mm});
            skLineSegment(sketch, "E175.0.86", {"start": v(-0.4, -9.3) * mm, "end": v(-0.2, -9.5) * mm});
            skArc(sketch, "E175.0.87", {"start": v(-0.2, -9.5) * mm, "mid": v(0, -9.5) * mm, "end": v(0.2, -9.5) * mm});
            skLineSegment(sketch, "E175.0.88", {"start": v(0.2, -9.5) * mm, "end": v(0.4, -9.3) * mm});
            skArc(sketch, "E175.0.89", {"start": v(0.4, -9.3) * mm, "mid": v(0.97, -9.25) * mm, "end": v(1.53, -9.17) * mm});
            skLineSegment(sketch, "E175.0.90", {"start": v(1.53, -9.17) * mm, "end": v(1.78, -9.33) * mm});
            skArc(sketch, "E175.0.91", {"start": v(1.78, -9.33) * mm, "mid": v(1.98, -9.3) * mm, "end": v(2.17, -9.25) * mm});
            skLineSegment(sketch, "E175.0.92", {"start": v(2.17, -9.25) * mm, "end": v(2.33, -9) * mm});
            skArc(sketch, "E175.0.93", {"start": v(2.33, -9) * mm, "mid": v(2.87, -8.84) * mm, "end": v(3.4, -8.65) * mm});
            skLineSegment(sketch, "E175.0.94", {"start": v(3.4, -8.65) * mm, "end": v(3.68, -8.76) * mm});
            skArc(sketch, "E175.0.95", {"start": v(3.68, -8.76) * mm, "mid": v(3.86, -8.68) * mm, "end": v(4.05, -8.6) * mm});
            skLineSegment(sketch, "E175.0.96", {"start": v(4.05, -8.6) * mm, "end": v(4.15, -8.32) * mm});
            skArc(sketch, "E175.0.97", {"start": v(4.15, -8.32) * mm, "mid": v(4.65, -8.05) * mm, "end": v(5.13, -7.76) * mm});
            skLineSegment(sketch, "E175.0.98", {"start": v(5.13, -7.76) * mm, "end": v(5.42, -7.8) * mm});
            skArc(sketch, "E175.0.99", {"start": v(5.42, -7.8) * mm, "mid": v(5.58, -7.69) * mm, "end": v(5.74, -7.57) * mm});
            skLineSegment(sketch, "E175.0.100", {"start": v(5.74, -7.57) * mm, "end": v(5.8, -7.28) * mm});
            skArc(sketch, "E175.0.101", {"start": v(5.8, -7.28) * mm, "mid": v(6.22, -6.91) * mm, "end": v(6.63, -6.52) * mm});
            skLineSegment(sketch, "E175.0.102", {"start": v(6.63, -6.52) * mm, "end": v(6.92, -6.5) * mm});
            skArc(sketch, "E175.0.103", {"start": v(6.92, -6.5) * mm, "mid": v(7.06, -6.36) * mm, "end": v(7.2, -6.2) * mm});
            skLineSegment(sketch, "E175.0.104", {"start": v(7.2, -6.2) * mm, "end": v(7.18, -5.91) * mm});
            skArc(sketch, "E175.0.105", {"start": v(7.18, -5.91) * mm, "mid": v(7.52, -5.47) * mm, "end": v(7.84, -5) * mm});
            skLineSegment(sketch, "E175.0.106", {"start": v(7.84, -5) * mm, "end": v(8.13, -4.92) * mm});
            skArc(sketch, "E175.0.107", {"start": v(8.13, -4.92) * mm, "mid": v(8.23, -4.75) * mm, "end": v(8.33, -4.58) * mm});
            skLineSegment(sketch, "E175.0.108", {"start": v(8.33, -4.58) * mm, "end": v(8.25, -4.3) * mm});
            skArc(sketch, "E175.0.109", {"start": v(8.25, -4.3) * mm, "mid": v(8.5, -3.78) * mm, "end": v(8.71, -3.26) * mm});
            skLineSegment(sketch, "E175.0.110", {"start": v(8.71, -3.26) * mm, "end": v(8.97, -3.13) * mm});
            skArc(sketch, "E175.0.111", {"start": v(8.97, -3.13) * mm, "mid": v(9.04, -2.94) * mm, "end": v(9.1, -2.74) * mm});
            skLineSegment(sketch, "E175.0.112", {"start": v(9.1, -2.74) * mm, "end": v(8.96, -2.48) * mm});
            skArc(sketch, "E175.0.113", {"start": v(8.96, -2.48) * mm, "mid": v(9.1, -1.93) * mm, "end": v(9.2, -1.38) * mm});
            skLineSegment(sketch, "E175.0.114", {"start": v(9.2, -1.38) * mm, "end": v(9.42, -1.2) * mm});
            skArc(sketch, "E175.0.115", {"start": v(9.42, -1.2) * mm, "mid": v(9.45, -1) * mm, "end": v(9.47, -0.8) * mm});
            skLineSegment(sketch, "E175.0.116", {"start": v(9.47, -0.8) * mm, "end": v(9.28, -0.57) * mm});
            skArc(sketch, "E175.0.117", {"start": v(9.28, -0.57) * mm, "mid": v(9.3, 0) * mm, "end": v(9.28, 0.57) * mm});
            skLineSegment(sketch, "E175.0.118", {"start": v(9.28, 0.57) * mm, "end": v(9.47, 0.8) * mm});
            skArc(sketch, "E175.0.119", {"start": v(9.47, 0.8) * mm, "mid": v(9.45, 1) * mm, "end": v(9.42, 1.2) * mm});
            skSolve(sketch);
        }
        {
            var Q0;
            Q0=makeQuery(id+"F6.imprint","IMPRINT",FACE,{"disambiguationData":[TD([[makeQuery(id+"F6.imprint","IMPRINT",EDGE,{"derivedFrom":sQuery(id+"F6.wireOp",EDGE,"E175.0.0")}),-1.0]])]});
            extrude(context, id + "F7", {"entities" : qUnion([Q0]), "operationType" : NewBodyOperationType.ADD, "depth" : (getVariable(context, 'Bore_Depth_F')) * mm});
        }
        {
            var Q0;
            Q0=makeQuery(id+"F7.opExtrude","CAP_FACE",FACE,{"disambiguationData":[OSD([sQuery(id+"F6.wireOp",EDGE,"E174"),sQuery(id+"F6.wireOp",EDGE,"E175.0.0"),sQuery(id+"F6.wireOp",EDGE,"E175.0.1"),sQuery(id+"F6.wireOp",EDGE,"E175.0.2"),sQuery(id+"F6.wireOp",EDGE,"E175.0.3"),sQuery(id+"F6.wireOp",EDGE,"E175.0.4"),sQuery(id+"F6.wireOp",EDGE,"E175.0.5"),sQuery(id+"F6.wireOp",EDGE,"E175.0.6"),sQuery(id+"F6.wireOp",EDGE,"E175.0.7"),sQuery(id+"F6.wireOp",EDGE,"E175.0.8"),sQuery(id+"F6.wireOp",EDGE,"E175.0.9"),sQuery(id+"F6.wireOp",EDGE,"E175.0.10"),sQuery(id+"F6.wireOp",EDGE,"E175.0.11"),sQuery(id+"F6.wireOp",EDGE,"E175.0.12"),sQuery(id+"F6.wireOp",EDGE,"E175.0.13"),sQuery(id+"F6.wireOp",EDGE,"E175.0.14"),sQuery(id+"F6.wireOp",EDGE,"E175.0.15"),sQuery(id+"F6.wireOp",EDGE,"E175.0.16"),sQuery(id+"F6.wireOp",EDGE,"E175.0.17"),sQuery(id+"F6.wireOp",EDGE,"E175.0.18"),sQuery(id+"F6.wireOp",EDGE,"E175.0.19"),sQuery(id+"F6.wireOp",EDGE,"E175.0.20"),sQuery(id+"F6.wireOp",EDGE,"E175.0.21"),sQuery(id+"F6.wireOp",EDGE,"E175.0.22"),sQuery(id+"F6.wireOp",EDGE,"E175.0.23"),sQuery(id+"F6.wireOp",EDGE,"E175.0.24"),sQuery(id+"F6.wireOp",EDGE,"E175.0.25"),sQuery(id+"F6.wireOp",EDGE,"E175.0.26"),sQuery(id+"F6.wireOp",EDGE,"E175.0.27"),sQuery(id+"F6.wireOp",EDGE,"E175.0.28"),sQuery(id+"F6.wireOp",EDGE,"E175.0.29"),sQuery(id+"F6.wireOp",EDGE,"E175.0.30"),sQuery(id+"F6.wireOp",EDGE,"E175.0.31"),sQuery(id+"F6.wireOp",EDGE,"E175.0.32"),sQuery(id+"F6.wireOp",EDGE,"E175.0.33"),sQuery(id+"F6.wireOp",EDGE,"E175.0.34"),sQuery(id+"F6.wireOp",EDGE,"E175.0.35"),sQuery(id+"F6.wireOp",EDGE,"E175.0.36"),sQuery(id+"F6.wireOp",EDGE,"E175.0.37"),sQuery(id+"F6.wireOp",EDGE,"E175.0.38"),sQuery(id+"F6.wireOp",EDGE,"E175.0.39"),sQuery(id+"F6.wireOp",EDGE,"E175.0.40"),sQuery(id+"F6.wireOp",EDGE,"E175.0.41"),sQuery(id+"F6.wireOp",EDGE,"E175.0.42"),sQuery(id+"F6.wireOp",EDGE,"E175.0.43"),sQuery(id+"F6.wireOp",EDGE,"E175.0.44"),sQuery(id+"F6.wireOp",EDGE,"E175.0.45"),sQuery(id+"F6.wireOp",EDGE,"E175.0.46"),sQuery(id+"F6.wireOp",EDGE,"E175.0.47"),sQuery(id+"F6.wireOp",EDGE,"E175.0.48"),sQuery(id+"F6.wireOp",EDGE,"E175.0.49"),sQuery(id+"F6.wireOp",EDGE,"E175.0.50"),sQuery(id+"F6.wireOp",EDGE,"E175.0.51"),sQuery(id+"F6.wireOp",EDGE,"E175.0.52"),sQuery(id+"F6.wireOp",EDGE,"E175.0.53"),sQuery(id+"F6.wireOp",EDGE,"E175.0.54"),sQuery(id+"F6.wireOp",EDGE,"E175.0.55"),sQuery(id+"F6.wireOp",EDGE,"E175.0.56"),sQuery(id+"F6.wireOp",EDGE,"E175.0.57"),sQuery(id+"F6.wireOp",EDGE,"E175.0.58"),sQuery(id+"F6.wireOp",EDGE,"E175.0.59"),sQuery(id+"F6.wireOp",EDGE,"E175.0.60"),sQuery(id+"F6.wireOp",EDGE,"E175.0.61"),sQuery(id+"F6.wireOp",EDGE,"E175.0.62"),sQuery(id+"F6.wireOp",EDGE,"E175.0.63"),sQuery(id+"F6.wireOp",EDGE,"E175.0.64"),sQuery(id+"F6.wireOp",EDGE,"E175.0.65"),sQuery(id+"F6.wireOp",EDGE,"E175.0.66"),sQuery(id+"F6.wireOp",EDGE,"E175.0.67"),sQuery(id+"F6.wireOp",EDGE,"E175.0.68"),sQuery(id+"F6.wireOp",EDGE,"E175.0.69"),sQuery(id+"F6.wireOp",EDGE,"E175.0.70"),sQuery(id+"F6.wireOp",EDGE,"E175.0.71"),sQuery(id+"F6.wireOp",EDGE,"E175.0.72"),sQuery(id+"F6.wireOp",EDGE,"E175.0.73"),sQuery(id+"F6.wireOp",EDGE,"E175.0.74"),sQuery(id+"F6.wireOp",EDGE,"E175.0.75"),sQuery(id+"F6.wireOp",EDGE,"E175.0.76"),sQuery(id+"F6.wireOp",EDGE,"E175.0.77"),sQuery(id+"F6.wireOp",EDGE,"E175.0.78"),sQuery(id+"F6.wireOp",EDGE,"E175.0.79"),sQuery(id+"F6.wireOp",EDGE,"E175.0.80"),sQuery(id+"F6.wireOp",EDGE,"E175.0.81"),sQuery(id+"F6.wireOp",EDGE,"E175.0.82"),sQuery(id+"F6.wireOp",EDGE,"E175.0.83"),sQuery(id+"F6.wireOp",EDGE,"E175.0.84"),sQuery(id+"F6.wireOp",EDGE,"E175.0.85"),sQuery(id+"F6.wireOp",EDGE,"E175.0.86"),sQuery(id+"F6.wireOp",EDGE,"E175.0.87"),sQuery(id+"F6.wireOp",EDGE,"E175.0.88"),sQuery(id+"F6.wireOp",EDGE,"E175.0.89"),sQuery(id+"F6.wireOp",EDGE,"E175.0.90"),sQuery(id+"F6.wireOp",EDGE,"E175.0.91"),sQuery(id+"F6.wireOp",EDGE,"E175.0.92"),sQuery(id+"F6.wireOp",EDGE,"E175.0.93"),sQuery(id+"F6.wireOp",EDGE,"E175.0.94"),sQuery(id+"F6.wireOp",EDGE,"E175.0.95"),sQuery(id+"F6.wireOp",EDGE,"E175.0.96"),sQuery(id+"F6.wireOp",EDGE,"E175.0.97"),sQuery(id+"F6.wireOp",EDGE,"E175.0.98"),sQuery(id+"F6.wireOp",EDGE,"E175.0.99"),sQuery(id+"F6.wireOp",EDGE,"E175.0.100"),sQuery(id+"F6.wireOp",EDGE,"E175.0.101"),sQuery(id+"F6.wireOp",EDGE,"E175.0.102"),sQuery(id+"F6.wireOp",EDGE,"E175.0.103"),sQuery(id+"F6.wireOp",EDGE,"E175.0.104"),sQuery(id+"F6.wireOp",EDGE,"E175.0.105"),sQuery(id+"F6.wireOp",EDGE,"E175.0.106"),sQuery(id+"F6.wireOp",EDGE,"E175.0.107"),sQuery(id+"F6.wireOp",EDGE,"E175.0.108"),sQuery(id+"F6.wireOp",EDGE,"E175.0.109"),sQuery(id+"F6.wireOp",EDGE,"E175.0.110"),sQuery(id+"F6.wireOp",EDGE,"E175.0.111"),sQuery(id+"F6.wireOp",EDGE,"E175.0.112"),sQuery(id+"F6.wireOp",EDGE,"E175.0.113"),sQuery(id+"F6.wireOp",EDGE,"E175.0.114"),sQuery(id+"F6.wireOp",EDGE,"E175.0.115"),sQuery(id+"F6.wireOp",EDGE,"E175.0.116"),sQuery(id+"F6.wireOp",EDGE,"E175.0.117"),sQuery(id+"F6.wireOp",EDGE,"E175.0.118"),sQuery(id+"F6.wireOp",EDGE,"E175.0.119")])],"isStart":false});
            var sketch = newSketch(context, id + "F8", { "sketchPlane" : qUnion([Q0])});
            skCircle(sketch, "E176", {"center": v(0, 0) * mm, "radius": 8 * mm});
            skCircle(sketch, "E177", {"center": v(0, 0) * mm, "radius": 9.5 * mm});
            skSolve(sketch);
        }
        {
            var Q0;
            Q0 = qSketchRegion(id + "F8", true);
            extrude(context, id + "F9", {"entities" : qUnion([Q0]), "oppositeDirection" : true, "depth" : (getVariable(context, 'Main_Length')) * mm});
        }
        {
            var Q0;
            Q0=makeQuery(id+"F5.opExtrude","CAP_FACE",FACE,{"disambiguationData":[OSD([sQuery(id+"F4.wireOp",EDGE,"E0"),sQuery(id+"F4.wireOp",EDGE,"E1"),sQuery(id+"F4.wireOp",EDGE,"E2"),sQuery(id+"F4.wireOp",EDGE,"E3"),sQuery(id+"F4.wireOp",EDGE,"E4"),sQuery(id+"F4.wireOp",EDGE,"E5"),sQuery(id+"F4.wireOp",EDGE,"E6"),sQuery(id+"F4.wireOp",EDGE,"E7"),sQuery(id+"F4.wireOp",EDGE,"E8"),sQuery(id+"F4.wireOp",EDGE,"E9"),sQuery(id+"F4.wireOp",EDGE,"E10"),sQuery(id+"F4.wireOp",EDGE,"E11"),sQuery(id+"F4.wireOp",EDGE,"E12"),sQuery(id+"F4.wireOp",EDGE,"E13"),sQuery(id+"F4.wireOp",EDGE,"E14"),sQuery(id+"F4.wireOp",EDGE,"E15"),sQuery(id+"F4.wireOp",EDGE,"E16"),sQuery(id+"F4.wireOp",EDGE,"E17"),sQuery(id+"F4.wireOp",EDGE,"E18"),sQuery(id+"F4.wireOp",EDGE,"E19"),sQuery(id+"F4.wireOp",EDGE,"E20"),sQuery(id+"F4.wireOp",EDGE,"E21"),sQuery(id+"F4.wireOp",EDGE,"E22"),sQuery(id+"F4.wireOp",EDGE,"E23"),sQuery(id+"F4.wireOp",EDGE,"E24"),sQuery(id+"F4.wireOp",EDGE,"E25"),sQuery(id+"F4.wireOp",EDGE,"E26"),sQuery(id+"F4.wireOp",EDGE,"E27"),sQuery(id+"F4.wireOp",EDGE,"E28"),sQuery(id+"F4.wireOp",EDGE,"E29"),sQuery(id+"F4.wireOp",EDGE,"E30"),sQuery(id+"F4.wireOp",EDGE,"E31"),sQuery(id+"F4.wireOp",EDGE,"E32"),sQuery(id+"F4.wireOp",EDGE,"E33"),sQuery(id+"F4.wireOp",EDGE,"E34"),sQuery(id+"F4.wireOp",EDGE,"E35"),sQuery(id+"F4.wireOp",EDGE,"E36"),sQuery(id+"F4.wireOp",EDGE,"E37"),sQuery(id+"F4.wireOp",EDGE,"E38"),sQuery(id+"F4.wireOp",EDGE,"E39"),sQuery(id+"F4.wireOp",EDGE,"E40"),sQuery(id+"F4.wireOp",EDGE,"E41"),sQuery(id+"F4.wireOp",EDGE,"E42"),sQuery(id+"F4.wireOp",EDGE,"E43"),sQuery(id+"F4.wireOp",EDGE,"E44"),sQuery(id+"F4.wireOp",EDGE,"E45"),sQuery(id+"F4.wireOp",EDGE,"E46"),sQuery(id+"F4.wireOp",EDGE,"E47"),sQuery(id+"F4.wireOp",EDGE,"E48"),sQuery(id+"F4.wireOp",EDGE,"E49"),sQuery(id+"F4.wireOp",EDGE,"E50"),sQuery(id+"F4.wireOp",EDGE,"E51"),sQuery(id+"F4.wireOp",EDGE,"E52"),sQuery(id+"F4.wireOp",EDGE,"E53"),sQuery(id+"F4.wireOp",EDGE,"E54"),sQuery(id+"F4.wireOp",EDGE,"E55"),sQuery(id+"F4.wireOp",EDGE,"E56"),sQuery(id+"F4.wireOp",EDGE,"E57"),sQuery(id+"F4.wireOp",EDGE,"E58"),sQuery(id+"F4.wireOp",EDGE,"E59"),sQuery(id+"F4.wireOp",EDGE,"E60"),sQuery(id+"F4.wireOp",EDGE,"E61"),sQuery(id+"F4.wireOp",EDGE,"E62"),sQuery(id+"F4.wireOp",EDGE,"E63"),sQuery(id+"F4.wireOp",EDGE,"E64"),sQuery(id+"F4.wireOp",EDGE,"E65"),sQuery(id+"F4.wireOp",EDGE,"E66"),sQuery(id+"F4.wireOp",EDGE,"E67"),sQuery(id+"F4.wireOp",EDGE,"E68"),sQuery(id+"F4.wireOp",EDGE,"E69"),sQuery(id+"F4.wireOp",EDGE,"E70"),sQuery(id+"F4.wireOp",EDGE,"E71"),sQuery(id+"F4.wireOp",EDGE,"E72"),sQuery(id+"F4.wireOp",EDGE,"E73"),sQuery(id+"F4.wireOp",EDGE,"E74"),sQuery(id+"F4.wireOp",EDGE,"E75"),sQuery(id+"F4.wireOp",EDGE,"E76"),sQuery(id+"F4.wireOp",EDGE,"E77"),sQuery(id+"F4.wireOp",EDGE,"E78"),sQuery(id+"F4.wireOp",EDGE,"E79"),sQuery(id+"F4.wireOp",EDGE,"E80"),sQuery(id+"F4.wireOp",EDGE,"E81"),sQuery(id+"F4.wireOp",EDGE,"E82"),sQuery(id+"F4.wireOp",EDGE,"E83"),sQuery(id+"F4.wireOp",EDGE,"E84"),sQuery(id+"F4.wireOp",EDGE,"E85"),sQuery(id+"F4.wireOp",EDGE,"E86"),sQuery(id+"F4.wireOp",EDGE,"E87"),sQuery(id+"F4.wireOp",EDGE,"E88"),sQuery(id+"F4.wireOp",EDGE,"E89"),sQuery(id+"F4.wireOp",EDGE,"E90"),sQuery(id+"F4.wireOp",EDGE,"E91"),sQuery(id+"F4.wireOp",EDGE,"E92"),sQuery(id+"F4.wireOp",EDGE,"E93"),sQuery(id+"F4.wireOp",EDGE,"E94"),sQuery(id+"F4.wireOp",EDGE,"E95"),sQuery(id+"F4.wireOp",EDGE,"E96"),sQuery(id+"F4.wireOp",EDGE,"E97"),sQuery(id+"F4.wireOp",EDGE,"E98"),sQuery(id+"F4.wireOp",EDGE,"E99"),sQuery(id+"F4.wireOp",EDGE,"E100"),sQuery(id+"F4.wireOp",EDGE,"E101"),sQuery(id+"F4.wireOp",EDGE,"E102"),sQuery(id+"F4.wireOp",EDGE,"E103"),sQuery(id+"F4.wireOp",EDGE,"E104"),sQuery(id+"F4.wireOp",EDGE,"E105"),sQuery(id+"F4.wireOp",EDGE,"E106"),sQuery(id+"F4.wireOp",EDGE,"E107"),sQuery(id+"F4.wireOp",EDGE,"E108"),sQuery(id+"F4.wireOp",EDGE,"E109"),sQuery(id+"F4.wireOp",EDGE,"E110"),sQuery(id+"F4.wireOp",EDGE,"E111"),sQuery(id+"F4.wireOp",EDGE,"E112"),sQuery(id+"F4.wireOp",EDGE,"E113"),sQuery(id+"F4.wireOp",EDGE,"E114"),sQuery(id+"F4.wireOp",EDGE,"E115"),sQuery(id+"F4.wireOp",EDGE,"E116"),sQuery(id+"F4.wireOp",EDGE,"E117"),sQuery(id+"F4.wireOp",EDGE,"E118"),sQuery(id+"F4.wireOp",EDGE,"E119"),sQuery(id+"F4.wireOp",EDGE,"E120"),sQuery(id+"F4.wireOp",EDGE,"E121"),sQuery(id+"F4.wireOp",EDGE,"E122"),sQuery(id+"F4.wireOp",EDGE,"E123"),sQuery(id+"F4.wireOp",EDGE,"E124"),sQuery(id+"F4.wireOp",EDGE,"E125"),sQuery(id+"F4.wireOp",EDGE,"E126"),sQuery(id+"F4.wireOp",EDGE,"E127"),sQuery(id+"F4.wireOp",EDGE,"E128"),sQuery(id+"F4.wireOp",EDGE,"E129"),sQuery(id+"F4.wireOp",EDGE,"E130"),sQuery(id+"F4.wireOp",EDGE,"E131"),sQuery(id+"F4.wireOp",EDGE,"E132"),sQuery(id+"F4.wireOp",EDGE,"E133"),sQuery(id+"F4.wireOp",EDGE,"E134"),sQuery(id+"F4.wireOp",EDGE,"E135"),sQuery(id+"F4.wireOp",EDGE,"E136"),sQuery(id+"F4.wireOp",EDGE,"E137"),sQuery(id+"F4.wireOp",EDGE,"E138"),sQuery(id+"F4.wireOp",EDGE,"E139"),sQuery(id+"F4.wireOp",EDGE,"E140"),sQuery(id+"F4.wireOp",EDGE,"E141"),sQuery(id+"F4.wireOp",EDGE,"E142"),sQuery(id+"F4.wireOp",EDGE,"E143"),sQuery(id+"F4.wireOp",EDGE,"E144"),sQuery(id+"F4.wireOp",EDGE,"E145"),sQuery(id+"F4.wireOp",EDGE,"E146"),sQuery(id+"F4.wireOp",EDGE,"E147"),sQuery(id+"F4.wireOp",EDGE,"E148"),sQuery(id+"F4.wireOp",EDGE,"E149"),sQuery(id+"F4.wireOp",EDGE,"E150"),sQuery(id+"F4.wireOp",EDGE,"E151"),sQuery(id+"F4.wireOp",EDGE,"E152"),sQuery(id+"F4.wireOp",EDGE,"E153"),sQuery(id+"F4.wireOp",EDGE,"E154"),sQuery(id+"F4.wireOp",EDGE,"E155"),sQuery(id+"F4.wireOp",EDGE,"E156"),sQuery(id+"F4.wireOp",EDGE,"E157"),sQuery(id+"F4.wireOp",EDGE,"E158"),sQuery(id+"F4.wireOp",EDGE,"E159"),sQuery(id+"F4.wireOp",EDGE,"E160"),sQuery(id+"F4.wireOp",EDGE,"E161"),sQuery(id+"F4.wireOp",EDGE,"E162"),sQuery(id+"F4.wireOp",EDGE,"E163"),sQuery(id+"F4.wireOp",EDGE,"E164"),sQuery(id+"F4.wireOp",EDGE,"E165"),sQuery(id+"F4.wireOp",EDGE,"E166"),sQuery(id+"F4.wireOp",EDGE,"E167"),sQuery(id+"F4.wireOp",EDGE,"E168"),sQuery(id+"F4.wireOp",EDGE,"E169"),sQuery(id+"F4.wireOp",EDGE,"E170"),sQuery(id+"F4.wireOp",EDGE,"E171"),sQuery(id+"F4.wireOp",EDGE,"E172"),sQuery(id+"F4.wireOp",EDGE,"E173")])],"isStart":true});
            var sketch = newSketch(context, id + "F10", { "sketchPlane" : qUnion([Q0])});
            skCircle(sketch, "E178", {"center": v(0, 0) * mm, "radius": 8 * mm});
            skLineSegment(sketch, "E179.0.0", {"start": v(-9.2, 1.38) * mm, "end": v(-9.42, 1.2) * mm});
            skArc(sketch, "E179.0.1", {"start": v(-9.42, 1.2) * mm, "mid": v(-9.45, 1) * mm, "end": v(-9.47, 0.8) * mm});
            skLineSegment(sketch, "E179.0.2", {"start": v(-9.47, 0.8) * mm, "end": v(-9.28, 0.57) * mm});
            skArc(sketch, "E179.0.3", {"start": v(-9.28, 0.57) * mm, "mid": v(-9.3, 0) * mm, "end": v(-9.28, -0.57) * mm});
            skLineSegment(sketch, "E179.0.4", {"start": v(-9.28, -0.57) * mm, "end": v(-9.47, -0.8) * mm});
            skArc(sketch, "E179.0.5", {"start": v(-9.47, -0.8) * mm, "mid": v(-9.45, -1) * mm, "end": v(-9.42, -1.2) * mm});
            skLineSegment(sketch, "E179.0.6", {"start": v(-9.42, -1.2) * mm, "end": v(-9.2, -1.38) * mm});
            skArc(sketch, "E179.0.7", {"start": v(-9.2, -1.38) * mm, "mid": v(-9.1, -1.93) * mm, "end": v(-8.96, -2.48) * mm});
            skLineSegment(sketch, "E179.0.8", {"start": v(-8.96, -2.48) * mm, "end": v(-9.1, -2.74) * mm});
            skArc(sketch, "E179.0.9", {"start": v(-9.1, -2.74) * mm, "mid": v(-9.04, -2.94) * mm, "end": v(-8.97, -3.13) * mm});
            skLineSegment(sketch, "E179.0.10", {"start": v(-8.97, -3.13) * mm, "end": v(-8.71, -3.26) * mm});
            skArc(sketch, "E179.0.11", {"start": v(-8.71, -3.26) * mm, "mid": v(-8.5, -3.78) * mm, "end": v(-8.25, -4.3) * mm});
            skLineSegment(sketch, "E179.0.12", {"start": v(-8.25, -4.3) * mm, "end": v(-8.33, -4.58) * mm});
            skArc(sketch, "E179.0.13", {"start": v(-8.33, -4.58) * mm, "mid": v(-8.23, -4.75) * mm, "end": v(-8.13, -4.92) * mm});
            skLineSegment(sketch, "E179.0.14", {"start": v(-8.13, -4.92) * mm, "end": v(-7.84, -5) * mm});
            skArc(sketch, "E179.0.15", {"start": v(-7.84, -5) * mm, "mid": v(-7.52, -5.47) * mm, "end": v(-7.18, -5.91) * mm});
            skLineSegment(sketch, "E179.0.16", {"start": v(-7.18, -5.91) * mm, "end": v(-7.2, -6.2) * mm});
            skArc(sketch, "E179.0.17", {"start": v(-7.2, -6.2) * mm, "mid": v(-7.06, -6.36) * mm, "end": v(-6.92, -6.5) * mm});
            skLineSegment(sketch, "E179.0.18", {"start": v(-6.92, -6.5) * mm, "end": v(-6.63, -6.52) * mm});
            skArc(sketch, "E179.0.19", {"start": v(-6.63, -6.52) * mm, "mid": v(-6.22, -6.91) * mm, "end": v(-5.8, -7.28) * mm});
            skLineSegment(sketch, "E179.0.20", {"start": v(-5.8, -7.28) * mm, "end": v(-5.74, -7.57) * mm});
            skArc(sketch, "E179.0.21", {"start": v(-5.74, -7.57) * mm, "mid": v(-5.58, -7.69) * mm, "end": v(-5.42, -7.8) * mm});
            skLineSegment(sketch, "E179.0.22", {"start": v(-5.42, -7.8) * mm, "end": v(-5.13, -7.76) * mm});
            skArc(sketch, "E179.0.23", {"start": v(-5.13, -7.76) * mm, "mid": v(-4.65, -8.05) * mm, "end": v(-4.15, -8.32) * mm});
            skLineSegment(sketch, "E179.0.24", {"start": v(-4.15, -8.32) * mm, "end": v(-4.05, -8.6) * mm});
            skArc(sketch, "E179.0.25", {"start": v(-4.05, -8.6) * mm, "mid": v(-3.86, -8.68) * mm, "end": v(-3.68, -8.76) * mm});
            skLineSegment(sketch, "E179.0.26", {"start": v(-3.68, -8.76) * mm, "end": v(-3.4, -8.65) * mm});
            skArc(sketch, "E179.0.27", {"start": v(-3.4, -8.65) * mm, "mid": v(-2.87, -8.84) * mm, "end": v(-2.33, -9) * mm});
            skLineSegment(sketch, "E179.0.28", {"start": v(-2.33, -9) * mm, "end": v(-2.17, -9.25) * mm});
            skArc(sketch, "E179.0.29", {"start": v(-2.17, -9.25) * mm, "mid": v(-1.98, -9.3) * mm, "end": v(-1.78, -9.33) * mm});
            skLineSegment(sketch, "E179.0.30", {"start": v(-1.78, -9.33) * mm, "end": v(-1.53, -9.17) * mm});
            skArc(sketch, "E179.0.31", {"start": v(-1.53, -9.17) * mm, "mid": v(-0.97, -9.25) * mm, "end": v(-0.4, -9.3) * mm});
            skLineSegment(sketch, "E179.0.32", {"start": v(-0.4, -9.3) * mm, "end": v(-0.2, -9.5) * mm});
            skArc(sketch, "E179.0.33", {"start": v(-0.2, -9.5) * mm, "mid": v(0, -9.5) * mm, "end": v(0.2, -9.5) * mm});
            skLineSegment(sketch, "E179.0.34", {"start": v(0.2, -9.5) * mm, "end": v(0.4, -9.3) * mm});
            skArc(sketch, "E179.0.35", {"start": v(0.4, -9.3) * mm, "mid": v(0.97, -9.25) * mm, "end": v(1.53, -9.17) * mm});
            skLineSegment(sketch, "E179.0.36", {"start": v(1.53, -9.17) * mm, "end": v(1.78, -9.33) * mm});
            skArc(sketch, "E179.0.37", {"start": v(1.78, -9.33) * mm, "mid": v(1.98, -9.3) * mm, "end": v(2.17, -9.25) * mm});
            skLineSegment(sketch, "E179.0.38", {"start": v(2.17, -9.25) * mm, "end": v(2.33, -9) * mm});
            skArc(sketch, "E179.0.39", {"start": v(2.33, -9) * mm, "mid": v(2.87, -8.84) * mm, "end": v(3.4, -8.65) * mm});
            skLineSegment(sketch, "E179.0.40", {"start": v(3.4, -8.65) * mm, "end": v(3.68, -8.76) * mm});
            skArc(sketch, "E179.0.41", {"start": v(3.68, -8.76) * mm, "mid": v(3.86, -8.68) * mm, "end": v(4.05, -8.6) * mm});
            skLineSegment(sketch, "E179.0.42", {"start": v(4.05, -8.6) * mm, "end": v(4.15, -8.32) * mm});
            skArc(sketch, "E179.0.43", {"start": v(4.15, -8.32) * mm, "mid": v(4.65, -8.05) * mm, "end": v(5.13, -7.76) * mm});
            skLineSegment(sketch, "E179.0.44", {"start": v(5.13, -7.76) * mm, "end": v(5.42, -7.8) * mm});
            skArc(sketch, "E179.0.45", {"start": v(5.42, -7.8) * mm, "mid": v(5.58, -7.69) * mm, "end": v(5.74, -7.57) * mm});
            skLineSegment(sketch, "E179.0.46", {"start": v(5.74, -7.57) * mm, "end": v(5.8, -7.28) * mm});
            skArc(sketch, "E179.0.47", {"start": v(5.8, -7.28) * mm, "mid": v(6.22, -6.91) * mm, "end": v(6.63, -6.52) * mm});
            skLineSegment(sketch, "E179.0.48", {"start": v(6.63, -6.52) * mm, "end": v(6.92, -6.5) * mm});
            skArc(sketch, "E179.0.49", {"start": v(6.92, -6.5) * mm, "mid": v(7.06, -6.36) * mm, "end": v(7.2, -6.2) * mm});
            skLineSegment(sketch, "E179.0.50", {"start": v(7.2, -6.2) * mm, "end": v(7.18, -5.91) * mm});
            skArc(sketch, "E179.0.51", {"start": v(7.18, -5.91) * mm, "mid": v(7.52, -5.47) * mm, "end": v(7.84, -5) * mm});
            skLineSegment(sketch, "E179.0.52", {"start": v(7.84, -5) * mm, "end": v(8.13, -4.92) * mm});
            skArc(sketch, "E179.0.53", {"start": v(8.13, -4.92) * mm, "mid": v(8.23, -4.75) * mm, "end": v(8.33, -4.58) * mm});
            skLineSegment(sketch, "E179.0.54", {"start": v(8.33, -4.58) * mm, "end": v(8.25, -4.3) * mm});
            skArc(sketch, "E179.0.55", {"start": v(8.25, -4.3) * mm, "mid": v(8.5, -3.78) * mm, "end": v(8.71, -3.26) * mm});
            skLineSegment(sketch, "E179.0.56", {"start": v(8.71, -3.26) * mm, "end": v(8.97, -3.13) * mm});
            skArc(sketch, "E179.0.57", {"start": v(8.97, -3.13) * mm, "mid": v(9.04, -2.94) * mm, "end": v(9.1, -2.74) * mm});
            skLineSegment(sketch, "E179.0.58", {"start": v(9.1, -2.74) * mm, "end": v(8.96, -2.48) * mm});
            skArc(sketch, "E179.0.59", {"start": v(8.96, -2.48) * mm, "mid": v(9.1, -1.93) * mm, "end": v(9.2, -1.38) * mm});
            skLineSegment(sketch, "E179.0.60", {"start": v(9.2, -1.38) * mm, "end": v(9.42, -1.2) * mm});
            skArc(sketch, "E179.0.61", {"start": v(9.42, -1.2) * mm, "mid": v(9.45, -1) * mm, "end": v(9.47, -0.8) * mm});
            skLineSegment(sketch, "E179.0.62", {"start": v(9.47, -0.8) * mm, "end": v(9.28, -0.57) * mm});
            skArc(sketch, "E179.0.63", {"start": v(9.28, -0.57) * mm, "mid": v(9.3, 0) * mm, "end": v(9.28, 0.57) * mm});
            skLineSegment(sketch, "E179.0.64", {"start": v(9.28, 0.57) * mm, "end": v(9.47, 0.8) * mm});
            skArc(sketch, "E179.0.65", {"start": v(9.47, 0.8) * mm, "mid": v(9.45, 1) * mm, "end": v(9.42, 1.2) * mm});
            skLineSegment(sketch, "E179.0.66", {"start": v(9.42, 1.2) * mm, "end": v(9.2, 1.38) * mm});
            skArc(sketch, "E179.0.67", {"start": v(9.2, 1.38) * mm, "mid": v(9.1, 1.93) * mm, "end": v(8.96, 2.48) * mm});
            skLineSegment(sketch, "E179.0.68", {"start": v(8.96, 2.48) * mm, "end": v(9.1, 2.74) * mm});
            skArc(sketch, "E179.0.69", {"start": v(9.1, 2.74) * mm, "mid": v(9.04, 2.94) * mm, "end": v(8.97, 3.13) * mm});
            skLineSegment(sketch, "E179.0.70", {"start": v(8.97, 3.13) * mm, "end": v(8.71, 3.26) * mm});
            skArc(sketch, "E179.0.71", {"start": v(8.71, 3.26) * mm, "mid": v(8.5, 3.78) * mm, "end": v(8.25, 4.3) * mm});
            skLineSegment(sketch, "E179.0.72", {"start": v(8.25, 4.3) * mm, "end": v(8.33, 4.58) * mm});
            skArc(sketch, "E179.0.73", {"start": v(8.33, 4.58) * mm, "mid": v(8.23, 4.75) * mm, "end": v(8.13, 4.92) * mm});
            skLineSegment(sketch, "E179.0.74", {"start": v(8.13, 4.92) * mm, "end": v(7.84, 5) * mm});
            skArc(sketch, "E179.0.75", {"start": v(7.84, 5) * mm, "mid": v(7.52, 5.47) * mm, "end": v(7.18, 5.91) * mm});
            skLineSegment(sketch, "E179.0.76", {"start": v(7.18, 5.91) * mm, "end": v(7.2, 6.2) * mm});
            skArc(sketch, "E179.0.77", {"start": v(7.2, 6.2) * mm, "mid": v(7.06, 6.36) * mm, "end": v(6.92, 6.5) * mm});
            skLineSegment(sketch, "E179.0.78", {"start": v(6.92, 6.5) * mm, "end": v(6.63, 6.52) * mm});
            skArc(sketch, "E179.0.79", {"start": v(6.63, 6.52) * mm, "mid": v(6.22, 6.91) * mm, "end": v(5.8, 7.28) * mm});
            skLineSegment(sketch, "E179.0.80", {"start": v(5.8, 7.28) * mm, "end": v(5.74, 7.57) * mm});
            skArc(sketch, "E179.0.81", {"start": v(5.74, 7.57) * mm, "mid": v(5.58, 7.69) * mm, "end": v(5.42, 7.8) * mm});
            skLineSegment(sketch, "E179.0.82", {"start": v(5.42, 7.8) * mm, "end": v(5.13, 7.76) * mm});
            skArc(sketch, "E179.0.83", {"start": v(5.13, 7.76) * mm, "mid": v(4.65, 8.05) * mm, "end": v(4.15, 8.32) * mm});
            skLineSegment(sketch, "E179.0.84", {"start": v(4.15, 8.32) * mm, "end": v(4.05, 8.6) * mm});
            skArc(sketch, "E179.0.85", {"start": v(4.05, 8.6) * mm, "mid": v(3.86, 8.68) * mm, "end": v(3.68, 8.76) * mm});
            skLineSegment(sketch, "E179.0.86", {"start": v(3.68, 8.76) * mm, "end": v(3.4, 8.65) * mm});
            skArc(sketch, "E179.0.87", {"start": v(3.4, 8.65) * mm, "mid": v(2.87, 8.84) * mm, "end": v(2.33, 9) * mm});
            skLineSegment(sketch, "E179.0.88", {"start": v(2.33, 9) * mm, "end": v(2.17, 9.25) * mm});
            skArc(sketch, "E179.0.89", {"start": v(2.17, 9.25) * mm, "mid": v(1.98, 9.3) * mm, "end": v(1.78, 9.33) * mm});
            skLineSegment(sketch, "E179.0.90", {"start": v(1.78, 9.33) * mm, "end": v(1.53, 9.17) * mm});
            skArc(sketch, "E179.0.91", {"start": v(1.53, 9.17) * mm, "mid": v(0.97, 9.25) * mm, "end": v(0.4, 9.3) * mm});
            skLineSegment(sketch, "E179.0.92", {"start": v(0.4, 9.3) * mm, "end": v(0.2, 9.5) * mm});
            skArc(sketch, "E179.0.93", {"start": v(0.2, 9.5) * mm, "mid": v(0, 9.5) * mm, "end": v(-0.2, 9.5) * mm});
            skLineSegment(sketch, "E179.0.94", {"start": v(-0.2, 9.5) * mm, "end": v(-0.4, 9.3) * mm});
            skArc(sketch, "E179.0.95", {"start": v(-0.4, 9.3) * mm, "mid": v(-0.97, 9.25) * mm, "end": v(-1.53, 9.17) * mm});
            skLineSegment(sketch, "E179.0.96", {"start": v(-1.53, 9.17) * mm, "end": v(-1.78, 9.33) * mm});
            skArc(sketch, "E179.0.97", {"start": v(-1.78, 9.33) * mm, "mid": v(-1.98, 9.3) * mm, "end": v(-2.17, 9.25) * mm});
            skLineSegment(sketch, "E179.0.98", {"start": v(-2.17, 9.25) * mm, "end": v(-2.33, 9) * mm});
            skArc(sketch, "E179.0.99", {"start": v(-2.33, 9) * mm, "mid": v(-2.87, 8.84) * mm, "end": v(-3.4, 8.65) * mm});
            skLineSegment(sketch, "E179.0.100", {"start": v(-3.4, 8.65) * mm, "end": v(-3.68, 8.76) * mm});
            skArc(sketch, "E179.0.101", {"start": v(-3.68, 8.76) * mm, "mid": v(-3.86, 8.68) * mm, "end": v(-4.05, 8.6) * mm});
            skLineSegment(sketch, "E179.0.102", {"start": v(-4.05, 8.6) * mm, "end": v(-4.15, 8.32) * mm});
            skArc(sketch, "E179.0.103", {"start": v(-4.15, 8.32) * mm, "mid": v(-4.65, 8.05) * mm, "end": v(-5.13, 7.76) * mm});
            skLineSegment(sketch, "E179.0.104", {"start": v(-5.13, 7.76) * mm, "end": v(-5.42, 7.8) * mm});
            skArc(sketch, "E179.0.105", {"start": v(-5.42, 7.8) * mm, "mid": v(-5.58, 7.69) * mm, "end": v(-5.74, 7.57) * mm});
            skLineSegment(sketch, "E179.0.106", {"start": v(-5.74, 7.57) * mm, "end": v(-5.8, 7.28) * mm});
            skArc(sketch, "E179.0.107", {"start": v(-5.8, 7.28) * mm, "mid": v(-6.22, 6.91) * mm, "end": v(-6.63, 6.52) * mm});
            skLineSegment(sketch, "E179.0.108", {"start": v(-6.63, 6.52) * mm, "end": v(-6.92, 6.5) * mm});
            skArc(sketch, "E179.0.109", {"start": v(-6.92, 6.5) * mm, "mid": v(-7.06, 6.36) * mm, "end": v(-7.2, 6.2) * mm});
            skLineSegment(sketch, "E179.0.110", {"start": v(-7.2, 6.2) * mm, "end": v(-7.18, 5.91) * mm});
            skArc(sketch, "E179.0.111", {"start": v(-7.18, 5.91) * mm, "mid": v(-7.52, 5.47) * mm, "end": v(-7.84, 5) * mm});
            skLineSegment(sketch, "E179.0.112", {"start": v(-7.84, 5) * mm, "end": v(-8.13, 4.92) * mm});
            skArc(sketch, "E179.0.113", {"start": v(-8.13, 4.92) * mm, "mid": v(-8.23, 4.75) * mm, "end": v(-8.33, 4.58) * mm});
            skLineSegment(sketch, "E179.0.114", {"start": v(-8.33, 4.58) * mm, "end": v(-8.25, 4.3) * mm});
            skArc(sketch, "E179.0.115", {"start": v(-8.25, 4.3) * mm, "mid": v(-8.5, 3.78) * mm, "end": v(-8.71, 3.26) * mm});
            skLineSegment(sketch, "E179.0.116", {"start": v(-8.71, 3.26) * mm, "end": v(-8.97, 3.13) * mm});
            skArc(sketch, "E179.0.117", {"start": v(-8.97, 3.13) * mm, "mid": v(-9.04, 2.94) * mm, "end": v(-9.1, 2.74) * mm});
            skLineSegment(sketch, "E179.0.118", {"start": v(-9.1, 2.74) * mm, "end": v(-8.96, 2.48) * mm});
            skArc(sketch, "E179.0.119", {"start": v(-8.96, 2.48) * mm, "mid": v(-9.1, 1.93) * mm, "end": v(-9.2, 1.38) * mm});
            skSolve(sketch);
        }
        {
            var Q0;
            Q0=makeQuery(id+"F10.imprint","IMPRINT",FACE,{"disambiguationData":[TD([[makeQuery(id+"F10.imprint","IMPRINT",EDGE,{"derivedFrom":sQuery(id+"F10.wireOp",EDGE,"E179.0.0")}),1.0]])]});
            extrude(context, id + "F11", {"entities" : qUnion([Q0]), "operationType" : NewBodyOperationType.ADD, "depth" : (getVariable(context, 'Bore_Depth_R')) * mm});
        }
        {
            var Q0;
            Q0=qCreatedBy(makeId("Right.planeOp"),FACE);
            cPlane(context, id + "F12", {"entities" : qUnion([Q0]), "cplaneType" : CPlaneType.OFFSET, "offset" : (getVariable(context, 'Main_Diam')) / 2 * mm, "oppositeDirection" : true, "width" : 150 * mm, "height" : 150 * mm});
        }
        {
            var Q0;
            Q0=qCreatedBy(id+"F12.planeOp",FACE);
            var sketch = newSketch(context, id + "F13", { "sketchPlane" : qUnion([Q0])});
            skCircle(sketch, "E180", {"center": v(-65.5, 0) * mm, "radius": 1.5 * mm});
            skPoint(sketch, "E181", {"position": v(-56.13, 0) * mm});
            skSolve(sketch);
        }
        {
            var Q0;
            Q0=makeQuery(id+"F13.imprint","IMPRINT",FACE,{"disambiguationData":[TD([[makeQuery(id+"F13.imprint","IMPRINT",EDGE,{"derivedFrom":sQuery(id+"F13.wireOp",EDGE,"E180")}),1.0]])]});
            extrude(context, id + "F14", {"entities" : qUnion([Q0]), "operationType" : NewBodyOperationType.REMOVE, "depth" : 5 * mm});
        }
    });
